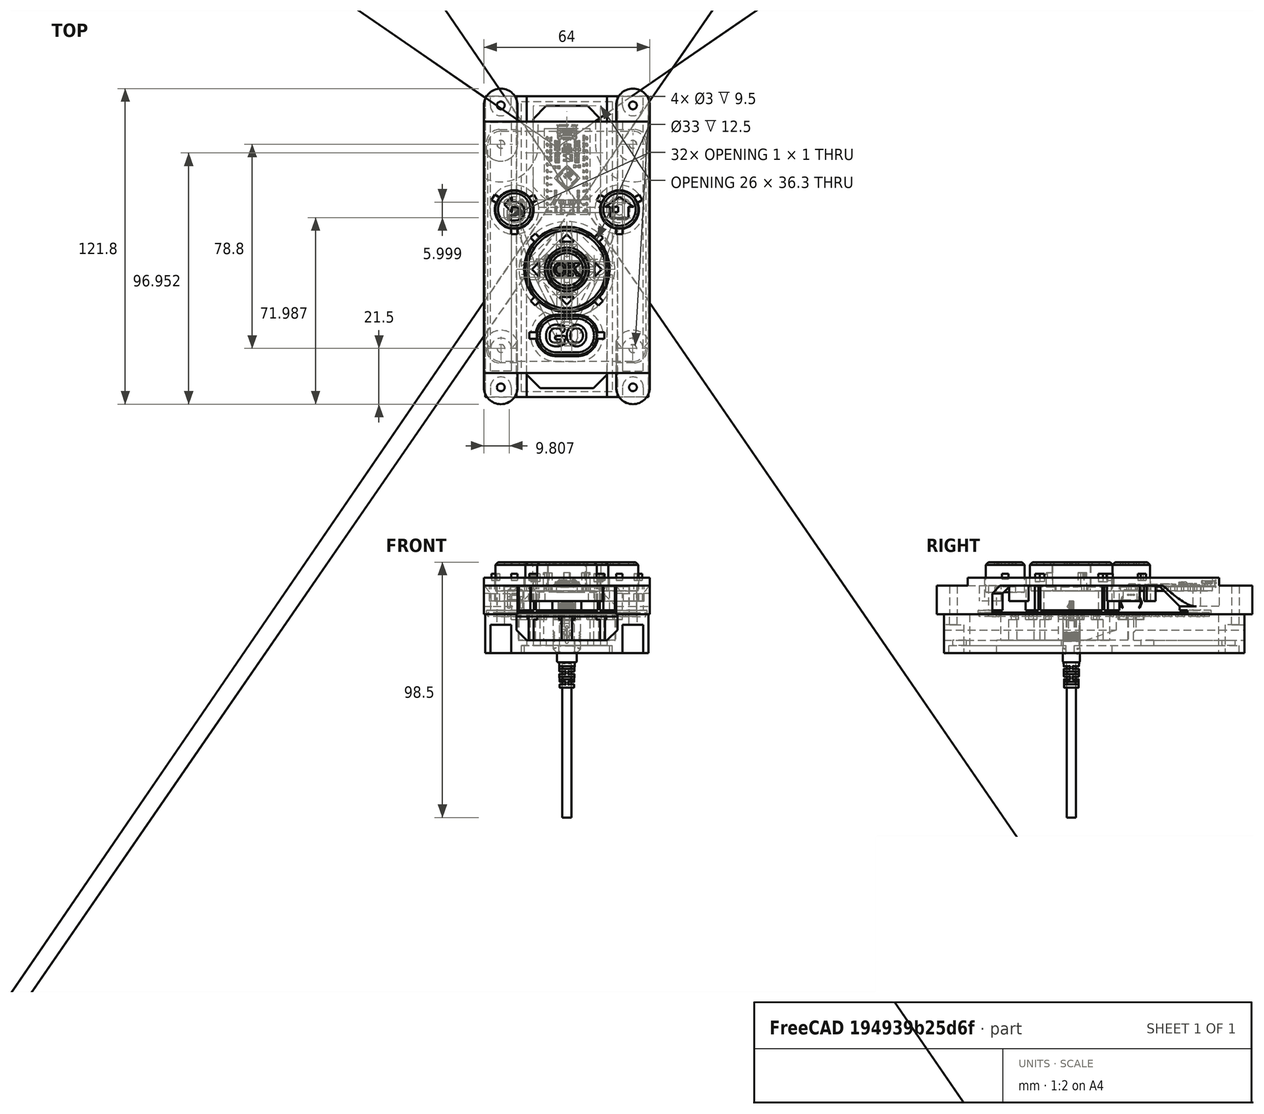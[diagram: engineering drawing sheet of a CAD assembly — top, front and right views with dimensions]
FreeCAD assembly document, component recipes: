
FREECAD ASSEMBLY — COMPONENT RECIPES ("NavigationBoard")

This assembly document has 11 components, labeled P0..P10 below (a component is one placed body or linked part). 7 of them carry a construction recipe — the FreeCAD feature program that regenerates the part from scratch, quoted from this document or its linked companion documents; the rest are supplied as boundary geometry only. No exploded tour is included for this assembly.
COMPONENT P0 — recipe-attached ("BoardHolder", modeled in this document).
Construction recipe (the document's own serialized feature program — sketch geometry with constraints, then the solid features built on it; lengths are millimeters unless a unit is written):

FEATURE [Sketcher::SketchObject] Sketch046
  ArcFitTolerance = 1e-06
  AttachmentSupport = -> [XY_Plane011]
  FullyConstrained = true
  MakeInternals = false
  MapMode = 5
  sketch-geometry (5):
    g0: LineSegment StartX=-31.5 StartY=-58 StartZ=0 EndX=31.5 EndY=-58 EndZ=0
    g1: LineSegment StartX=31.5 StartY=-58 StartZ=0 EndX=31.5 EndY=58 EndZ=0
    g2: LineSegment StartX=31.5 StartY=58 StartZ=0 EndX=-31.5 EndY=58 EndZ=0
    g3: LineSegment StartX=-31.5 StartY=58 StartZ=0 EndX=-31.5 EndY=-58 EndZ=0
    g4: GeomPoint [constr] X=0 Y=0 Z=0
  constraints (12):
    c: Coincident(g0,g1)
    c: Coincident(g1,g2)
    c: Coincident(g2,g3)
    c: Coincident(g3,g0)
    c: Horizontal(g0)
    c: Horizontal(g2)
    c: Vertical(g1)
    c: Vertical(g3)
    c: Symmetric(g2,g0,g4)
    c: Distance(g1,g3) = 63
    c: Distance(g0,g2) = 116
    c: Coincident(g4,g-1)
FEATURE [PartDesign::Pad] Pad025
  Direction = (0,0,1)
  Length = 5
  Length2 = 10
  Profile = -> Sketch046
  ReferenceAxis = -> Sketch046 [N_Axis]
  Refine = true
  Suppressed = false
  Type = 0
FEATURE [Sketcher::SketchObject] Sketch047
  ArcFitTolerance = 1e-06
  AttachmentSupport = -> [Pad025]
  FullyConstrained = true
  MakeInternals = false
  MapMode = 5
  Placement = pos=(0,0,5) rot=(0,0,1;0rad)
  sketch-geometry (8):
    g0: Circle CenterX=-20.3 CenterY=14.22 CenterZ=0 NormalX=0 NormalY=0 NormalZ=1 AngleXU=0 Radius=2
    g1: Circle CenterX=20.3 CenterY=14.22 CenterZ=0 NormalX=0 NormalY=0 NormalZ=1 AngleXU=0 Radius=2
    g2: Circle CenterX=0 CenterY=3.9 CenterZ=0 NormalX=0 NormalY=0 NormalZ=1 AngleXU=0 Radius=2
    g3: Circle CenterX=-12.7 CenterY=-8.8 CenterZ=0 NormalX=0 NormalY=0 NormalZ=1 AngleXU=0 Radius=2
    g4: Circle CenterX=0 CenterY=-8.8 CenterZ=0 NormalX=0 NormalY=0 NormalZ=1 AngleXU=0 Radius=2
    g5: Circle CenterX=12.7 CenterY=-8.8 CenterZ=0 NormalX=0 NormalY=0 NormalZ=1 AngleXU=0 Radius=2
    g6: Circle CenterX=0 CenterY=-21.5 CenterZ=0 NormalX=0 NormalY=0 NormalZ=1 AngleXU=0 Radius=2
    g7: Circle CenterX=0 CenterY=-34.1 CenterZ=0 NormalX=0 NormalY=0 NormalZ=1 AngleXU=0 Radius=2
  constraints (24):
    c: Diameter(g0) = 4
    c: DistanceX(g0,g-1) = 20.3
    c: Distance(g0,g-1) = 14.22
    c: Diameter(g1) = 4
    c: DistanceX(g-1,g1) = 20.3
    c: Distance(g1,g-1) = 14.22
    c: Diameter(g2) = 4
    c: PointOnObject(g2,g-2)
    c: DistanceY(g-1,g2) = 3.9
    c: Diameter(g3) = 4
    c: Diameter(g4) = 4
    c: PointOnObject(g4,g-2)
    c: Diameter(g5) = 4
    c: Distance(g3,g-2) = 12.7
    c: DistanceY(g3,g-1) = 8.8
    c: Horizontal(g3,g4)
    c: Horizontal(g4,g5)
    c: DistanceX(g-1,g5) = 12.7
    c: Diameter(g6) = 4
    c: PointOnObject(g6,g-2)
    c: Diameter(g7) = 4
    c: PointOnObject(g7,g-2)
    c: DistanceY(g6,g-1) = 21.5
    c: DistanceY(g7,g6) = 12.6
FEATURE [PartDesign::Pad] Pad026
  BaseFeature = -> Pad025
  Direction = (0,0,1)
  Length = 10
  Length2 = 10
  Profile = -> Sketch047
  ReferenceAxis = -> Sketch047 [N_Axis]
  Refine = true
  Suppressed = false
  Type = 0
FEATURE [Sketcher::SketchObject] Sketch048
  ArcFitTolerance = 1e-06
  AttachmentSupport = -> [Pad026]
  ExternalGeometry = -> [Pad026]
  FullyConstrained = false
  MakeInternals = false
  MapMode = 5
  Placement = pos=(0,0,5) rot=(0,0,1;0rad)
  sketch-geometry (15):
    g0: LineSegment StartX=-13.6496 StartY=-9.1135 StartZ=0 EndX=-21.2496 EndY=13.9065 EndZ=0
    g1: ArcOfCircle CenterX=-20.3 CenterY=14.22 CenterZ=0 NormalX=0 NormalY=0 NormalZ=1 AngleXU=0 Radius=1 StartAngle=1.5708 EndAngle=3.46047
    g2: LineSegment StartX=-20.3 StartY=15.22 StartZ=0 EndX=20.3 EndY=15.22 EndZ=0
    g3: ArcOfCircle CenterX=20.3 CenterY=14.22 CenterZ=0 NormalX=0 NormalY=0 NormalZ=1 AngleXU=-1.88968 Radius=1 StartAngle=1.5708 EndAngle=3.46047
    g4: LineSegment StartX=21.2496 StartY=13.9065 StartZ=0 EndX=13.6496 EndY=-9.1135 EndZ=0
    g5: ArcOfCircle CenterX=12.7 CenterY=-8.8 CenterZ=0 NormalX=0 NormalY=0 NormalZ=1 AngleXU=-2.03602 Radius=1 StartAngle=1.5708 EndAngle=1.71714
    g6: LineSegment StartX=13.5937 StartY=-9.24863 StartZ=0 EndX=0.89372 EndY=-34.5486 EndZ=0
    g7: ArcOfCircle CenterX=0 CenterY=-34.1 CenterZ=0 NormalX=0 NormalY=0 NormalZ=1 AngleXU=2.03602 Radius=1 StartAngle=1.5708 EndAngle=3.78193
    g8: LineSegment StartX=-0.89372 StartY=-34.5486 StartZ=0 EndX=-13.5937 EndY=-9.24863 EndZ=0
    g9: ArcOfCircle CenterX=-12.7 CenterY=-8.8 CenterZ=0 NormalX=0 NormalY=0 NormalZ=1 AngleXU=1.88968 Radius=1 StartAngle=1.5708 EndAngle=1.71714
    g10: LineSegment StartX=-11.7734 StartY=-8.41689 StartZ=0 EndX=-18.9168 EndY=13.22 EndZ=0
    g11: LineSegment StartX=-18.9168 StartY=13.22 StartZ=0 EndX=18.9168 EndY=13.22 EndZ=0
    g12: LineSegment StartX=18.9168 StartY=13.22 StartZ=0 EndX=11.7734 EndY=-8.41689 EndZ=0
    g13: LineSegment StartX=11.7734 StartY=-8.41689 StartZ=0 EndX=-1.8e-15 EndY=-31.871 EndZ=0
    g14: LineSegment StartX=-1.8e-15 StartY=-31.871 StartZ=0 EndX=-11.7734 EndY=-8.41689 EndZ=0
  constraints (15):
    c: Tangent(g0,g1) = 1.5708
    c: Tangent(g0,g9) = 1.5708
    c: Tangent(g1,g2) = 1.5708
    c: Tangent(g2,g3) = 1.5708
    c: Tangent(g3,g4) = 1.5708
    c: Tangent(g4,g5) = 1.5708
    c: Tangent(g5,g6) = 1.5708
    c: Tangent(g6,g7) = 1.5708
    c: Tangent(g7,g8) = 1.5708
    c: Tangent(g8,g9) = 1.5708
    c: Coincident(g10,g11)
    c: Coincident(g10,g14)
    c: Coincident(g11,g12)
    c: Coincident(g12,g13)
    c: Coincident(g13,g14)
FEATURE [PartDesign::Pad] Pad027
  BaseFeature = -> Pad026
  Direction = (0,0,1)
  Length = 10
  Length2 = 10
  Profile = -> Sketch048
  ReferenceAxis = -> Sketch048 [N_Axis]
  Refine = true
  Suppressed = false
  Type = 0
FEATURE [Sketcher::SketchObject] Sketch049
  ArcFitTolerance = 1e-06
  AttachmentSupport = -> [Pad027]
  ExternalGeometry = -> [Pad027]
  FullyConstrained = false
  MakeInternals = false
  MapMode = 5
  Placement = pos=(0,0,5) rot=(0,0,1;0rad)
  sketch-geometry (12):
    g0: LineSegment StartX=-13.4071 StartY=-9.50711 StartZ=0 EndX=-0.707107 EndY=-22.2071 EndZ=0
    g1: ArcOfCircle CenterX=0 CenterY=-21.5 CenterZ=0 NormalX=0 NormalY=0 NormalZ=-1 AngleXU=2.35619 Radius=1 StartAngle=1.5708 EndAngle=3.14159
    g2: LineSegment StartX=0.707107 StartY=-22.2071 StartZ=0 EndX=13.4071 EndY=-9.50711 EndZ=0
    g3: ArcOfCircle CenterX=12.7 CenterY=-8.8 CenterZ=0 NormalX=0 NormalY=0 NormalZ=-1 AngleXU=0.785398 Radius=1 StartAngle=1.5708 EndAngle=3.14159
    g4: LineSegment StartX=13.4071 StartY=-8.09289 StartZ=0 EndX=0.707107 EndY=4.60711 EndZ=0
    g5: ArcOfCircle CenterX=0 CenterY=3.9 CenterZ=0 NormalX=0 NormalY=0 NormalZ=-1 AngleXU=-0.785398 Radius=1 StartAngle=1.5708 EndAngle=3.14159
    g6: LineSegment StartX=-0.707107 StartY=4.60711 StartZ=0 EndX=-13.4071 EndY=-8.09289 EndZ=0
    g7: ArcOfCircle CenterX=-12.7 CenterY=-8.8 CenterZ=0 NormalX=0 NormalY=0 NormalZ=-1 AngleXU=-2.35619 Radius=1 StartAngle=1.5708 EndAngle=3.14159
    g8: LineSegment StartX=-11.2858 StartY=-8.8 StartZ=0 EndX=0 EndY=-20.0858 EndZ=0
    g9: LineSegment StartX=0 StartY=-20.0858 StartZ=0 EndX=11.2858 EndY=-8.8 EndZ=0
    g10: LineSegment StartX=11.2858 StartY=-8.8 StartZ=0 EndX=0 EndY=2.48579 EndZ=0
    g11: LineSegment StartX=0 StartY=2.48579 StartZ=0 EndX=-11.2858 EndY=-8.8 EndZ=0
  constraints (12):
    c: Tangent(g0,g1) = -1.5708
    c: Tangent(g0,g7) = -1.5708
    c: Tangent(g1,g2) = -1.5708
    c: Tangent(g2,g3) = -1.5708
    c: Tangent(g3,g4) = -1.5708
    c: Tangent(g4,g5) = -1.5708
    c: Tangent(g5,g6) = -1.5708
    c: Tangent(g6,g7) = -1.5708
    c: Coincident(g8,g9)
    c: Coincident(g8,g11)
    c: Coincident(g9,g10)
    c: Coincident(g10,g11)
FEATURE [PartDesign::Pad] Pad028
  BaseFeature = -> Pad027
  Direction = (0,0,1)
  Length = 10
  Length2 = 10
  Profile = -> Sketch049
  ReferenceAxis = -> Sketch049 [N_Axis]
  Refine = true
  Suppressed = false
  Type = 0
FEATURE [Sketcher::SketchObject] Sketch050
  ArcFitTolerance = 1e-06
  AttachmentSupport = -> [Pad028]
  ExternalGeometry = -> [Pad028]
  FullyConstrained = false
  MakeInternals = false
  MapMode = 5
  Placement = pos=(0,0,5) rot=(0,0,1;0rad)
  sketch-geometry (6):
    g0: ArcOfCircle CenterX=0 CenterY=3.9 CenterZ=0 NormalX=0 NormalY=0 NormalZ=-1 AngleXU=-1.5708 Radius=1 StartAngle=1.5708 EndAngle=4.71239
    g1: LineSegment StartX=1 StartY=3.9 StartZ=0 EndX=1 EndY=-8.76667 EndZ=0
    g2: LineSegment StartX=1 StartY=-8.76667 StartZ=0 EndX=1 EndY=-34.1 EndZ=0
    g3: ArcOfCircle CenterX=0 CenterY=-34.1 CenterZ=0 NormalX=0 NormalY=0 NormalZ=-1 AngleXU=1.5708 Radius=1 StartAngle=1.5708 EndAngle=4.71239
    g4: LineSegment StartX=-1 StartY=-8.76667 StartZ=0 EndX=-1 EndY=-34.1 EndZ=0
    g5: LineSegment StartX=-1 StartY=3.9 StartZ=0 EndX=-1 EndY=-8.76667 EndZ=0
  constraints (6):
    c: Tangent(g0,g1) = 1.5708
    c: Tangent(g0,g5) = -1.5708
    c: Coincident(g1,g2)
    c: Tangent(g2,g3) = 1.5708
    c: Tangent(g3,g4) = -1.5708
    c: Coincident(g4,g5)
FEATURE [PartDesign::Pad] Pad029
  BaseFeature = -> Pad028
  Direction = (0,0,1)
  Length = 10
  Length2 = 10
  Profile = -> Sketch050
  ReferenceAxis = -> Sketch050 [N_Axis]
  Refine = true
  Suppressed = false
  Type = 0
FEATURE [Sketcher::SketchObject] Sketch051
  ArcFitTolerance = 1e-06
  AttachmentSupport = -> [Pad029]
  ExternalGeometry = -> [Pad029]
  FullyConstrained = false
  MakeInternals = false
  MapMode = 5
  Placement = pos=(0,0,5) rot=(0,0,1;0rad)
  sketch-geometry (6):
    g0: ArcOfCircle CenterX=-12.7 CenterY=-8.8 CenterZ=0 NormalX=0 NormalY=0 NormalZ=-1 AngleXU=-3.14159 Radius=1 StartAngle=1.5708 EndAngle=4.71239
    g1: LineSegment StartX=-12.7 StartY=-7.8 StartZ=0 EndX=-4.23333 EndY=-7.8 EndZ=0
    g2: LineSegment StartX=-4.23333 StartY=-7.8 StartZ=0 EndX=12.7 EndY=-7.8 EndZ=0
    g3: ArcOfCircle CenterX=12.7 CenterY=-8.8 CenterZ=0 NormalX=0 NormalY=0 NormalZ=-1 AngleXU=0 Radius=1 StartAngle=1.5708 EndAngle=4.71239
    g4: LineSegment StartX=-4.23333 StartY=-9.8 StartZ=0 EndX=12.7 EndY=-9.8 EndZ=0
    g5: LineSegment StartX=-12.7 StartY=-9.8 StartZ=0 EndX=-4.23333 EndY=-9.8 EndZ=0
  constraints (6):
    c: Tangent(g0,g1) = 1.5708
    c: Tangent(g0,g5) = -1.5708
    c: Coincident(g1,g2)
    c: Tangent(g2,g3) = 1.5708
    c: Tangent(g3,g4) = -1.5708
    c: Coincident(g4,g5)
FEATURE [PartDesign::Pad] Pad030
  BaseFeature = -> Pad029
  Direction = (0,0,1)
  Length = 10
  Length2 = 10
  Profile = -> Sketch051
  ReferenceAxis = -> Sketch051 [N_Axis]
  Refine = true
  Suppressed = false
  Type = 0
FEATURE [Sketcher::SketchObject] Sketch052
  ArcFitTolerance = 1e-06
  AttachmentSupport = -> [Pad030]
  ExternalGeometry = -> [Pad030]
  FullyConstrained = true
  MakeInternals = false
  MapMode = 5
  Placement = pos=(0,0,15) rot=(0,0,1;0rad)
  sketch-geometry (16):
    g0: Circle CenterX=-20.3 CenterY=14.22 CenterZ=0 NormalX=0 NormalY=0 NormalZ=1 AngleXU=0 Radius=5
    g1: Circle CenterX=20.3 CenterY=14.22 CenterZ=0 NormalX=0 NormalY=0 NormalZ=1 AngleXU=0 Radius=5
    g2: Circle CenterX=0 CenterY=3.9 CenterZ=0 NormalX=0 NormalY=0 NormalZ=1 AngleXU=0 Radius=5
    g3: Circle CenterX=-12.7 CenterY=-8.8 CenterZ=0 NormalX=0 NormalY=0 NormalZ=1 AngleXU=0 Radius=5
    g4: Circle CenterX=0 CenterY=-8.8 CenterZ=0 NormalX=0 NormalY=0 NormalZ=1 AngleXU=0 Radius=5
    g5: Circle CenterX=12.7 CenterY=-8.8 CenterZ=0 NormalX=0 NormalY=0 NormalZ=1 AngleXU=0 Radius=5
    g6: Circle CenterX=0 CenterY=-21.5 CenterZ=0 NormalX=0 NormalY=0 NormalZ=1 AngleXU=0 Radius=5
    g7: Circle CenterX=-20.3 CenterY=14.22 CenterZ=0 NormalX=0 NormalY=0 NormalZ=1 AngleXU=0 Radius=2
    g8: Circle CenterX=20.3 CenterY=14.22 CenterZ=0 NormalX=0 NormalY=0 NormalZ=1 AngleXU=0 Radius=2
    g9: Circle CenterX=0 CenterY=3.9 CenterZ=0 NormalX=0 NormalY=0 NormalZ=1 AngleXU=0 Radius=2
    g10: Circle CenterX=-12.7 CenterY=-8.8 CenterZ=0 NormalX=0 NormalY=0 NormalZ=1 AngleXU=0 Radius=2
    g11: Circle CenterX=0 CenterY=-8.8 CenterZ=0 NormalX=0 NormalY=0 NormalZ=1 AngleXU=0 Radius=2
    g12: Circle CenterX=12.7 CenterY=-8.8 CenterZ=0 NormalX=0 NormalY=0 NormalZ=1 AngleXU=0 Radius=2
    g13: Circle CenterX=0 CenterY=-21.5 CenterZ=0 NormalX=0 NormalY=0 NormalZ=1 AngleXU=0 Radius=2
    g14: Circle CenterX=0 CenterY=-34.1 CenterZ=0 NormalX=0 NormalY=0 NormalZ=1 AngleXU=0 Radius=5
    g15: Circle CenterX=0 CenterY=-34.1 CenterZ=0 NormalX=0 NormalY=0 NormalZ=1 AngleXU=0 Radius=2
  constraints (32):
    c: Diameter(g0) = 10
    c: Coincident(g0,g-3)
    c: Diameter(g1) = 10
    c: Coincident(g1,g-4)
    c: Diameter(g2) = 10
    c: Coincident(g2,g-5)
    c: Diameter(g3) = 10
    c: Coincident(g3,g-6)
    c: Diameter(g4) = 10
    c: Coincident(g4,g-8)
    c: Diameter(g5) = 10
    c: Coincident(g5,g-7)
    c: Diameter(g6) = 10
    c: Coincident(g6,g-9)
    c: Diameter(g7) = 4
    c: Coincident(g7,g0)
    c: Diameter(g8) = 4
    c: Coincident(g8,g1)
    c: Diameter(g9) = 4
    c: Coincident(g9,g2)
    c: Diameter(g10) = 4
    c: Coincident(g10,g3)
    c: Diameter(g11) = 4
    c: Coincident(g11,g4)
    c: Diameter(g12) = 4
    c: Coincident(g12,g5)
    c: Diameter(g13) = 4
    c: Coincident(g13,g6)
    c: Diameter(g14) = 10
    c: Coincident(g14,g-10)
    c: Diameter(g15) = 4
    c: Coincident(g15,g14)
FEATURE [Sketcher::SketchObject] Sketch053
  ArcFitTolerance = 1e-06
  AttachmentSupport = -> [Pad030]
  FullyConstrained = true
  MakeInternals = false
  MapMode = 5
  Placement = pos=(31.5,0,0) rot=(0.57735,0.57735,0.57735;2.0944rad)
  sketch-geometry (4):
    g0: LineSegment StartX=-58 StartY=15 StartZ=0 EndX=-58 EndY=5 EndZ=0
    g1: LineSegment StartX=-58 StartY=5 StartZ=0 EndX=58 EndY=5 EndZ=0
    g2: LineSegment StartX=58 StartY=15 StartZ=0 EndX=-58 EndY=15 EndZ=0
    g3: LineSegment StartX=58 StartY=15 StartZ=0 EndX=58 EndY=5 EndZ=0
  constraints (12):
    c: Vertical(g0)
    c: PointOnObject(g1,g-3)
    c: PointOnObject(g1,g-3)
    c: Coincident(g2,g0)
    c: Horizontal(g2)
    c: Distance(g-2,g0) = 58
    c: Vertical(g3)
    c: DistanceY(g1,g2) = 10
    c: Distance(g-2,g3) = 58
    c: Coincident(g2,g3)
    c: Coincident(g0,g1)
    c: Coincident(g3,g1)
FEATURE [PartDesign::Pad] Pad031
  BaseFeature = -> Pad030
  Direction = (1,0,0)
  Length = 12
  Length2 = 10
  Profile = -> Sketch053
  ReferenceAxis = -> Sketch053 [N_Axis]
  Refine = true
  Reversed = true
  Suppressed = false
  Type = 0
FEATURE [Sketcher::SketchObject] Sketch054
  ArcFitTolerance = 1e-06
  AttachmentSupport = -> [Pad031]
  ExternalGeometry = -> [Pad031]
  FullyConstrained = true
  MakeInternals = false
  MapMode = 5
  Placement = pos=(0,0,15) rot=(0,0,1;0rad)
  sketch-geometry (6):
    g0: LineSegment StartX=21.5 StartY=48 StartZ=0 EndX=21.5 EndY=-48 EndZ=0
    g1: LineSegment StartX=21.5 StartY=-48 StartZ=0 EndX=29.5 EndY=-48 EndZ=0
    g2: LineSegment StartX=29.5 StartY=-48 StartZ=0 EndX=29.5 EndY=48 EndZ=0
    g3: LineSegment StartX=29.5 StartY=48 StartZ=0 EndX=21.5 EndY=48 EndZ=0
    g4: Circle CenterX=25.5 CenterY=-54.3 CenterZ=0 NormalX=0 NormalY=0 NormalZ=1 AngleXU=0 Radius=1.5
    g5: Circle CenterX=25.5 CenterY=54.5 CenterZ=0 NormalX=0 NormalY=0 NormalZ=1 AngleXU=0 Radius=1.5
  constraints (18):
    c: Coincident(g0,g1)
    c: Coincident(g1,g2)
    c: Coincident(g2,g3)
    c: Coincident(g3,g0)
    c: Vertical(g0)
    c: Vertical(g2)
    c: Horizontal(g1)
    c: Horizontal(g3)
    c: Distance(g-5,g3) = 10
    c: Distance(g-4,g0) = 2
    c: Distance(g-3,g2) = 2
    c: Distance(g-3,g1) = 10
    c: Diameter(g4) = 3
    c: Distance(g4,g-3) = 6
    c: DistanceY(g4,g1) = 6.3
    c: Diameter(g5) = 3
    c: Distance(g5,g-4) = 6
    c: Distance(g5,g3) = 6.5
FEATURE [PartDesign::Pocket] Pocket023
  BaseFeature = -> Pad031
  Direction = (0,0,-1)
  Length = 5
  Length2 = 5
  Profile = -> Sketch054
  ReferenceAxis = -> Sketch054 [N_Axis]
  Refine = true
  Suppressed = false
  Type = 1
FEATURE [Sketcher::SketchObject] Sketch055
  ArcFitTolerance = 1e-06
  AttachmentSupport = -> [Pocket023]
  ExternalGeometry = -> [Pocket023]
  FullyConstrained = true
  MakeInternals = false
  MapMode = 5
  Placement = pos=(0,0,0) rot=(1,0,0;3.14159rad)
  sketch-geometry (8):
    g0: ArcOfCircle CenterX=25.5 CenterY=54.3 CenterZ=0 NormalX=0 NormalY=0 NormalZ=1 AngleXU=0 Radius=4 StartAngle=3.14159 EndAngle=6.28319
    g1: ArcOfCircle CenterX=25.5 CenterY=62.3 CenterZ=0 NormalX=0 NormalY=0 NormalZ=1 AngleXU=0 Radius=4 StartAngle=0 EndAngle=3.14159
    g2: LineSegment StartX=21.5 StartY=54.3 StartZ=0 EndX=21.5 EndY=62.3 EndZ=0
    g3: LineSegment StartX=29.5 StartY=54.3 StartZ=0 EndX=29.5 EndY=62.3 EndZ=0
    g4: ArcOfCircle CenterX=25.5 CenterY=-54.5 CenterZ=0 NormalX=0 NormalY=0 NormalZ=1 AngleXU=0 Radius=4 StartAngle=-9e-16 EndAngle=3.14159
    g5: ArcOfCircle CenterX=25.5 CenterY=-62.5 CenterZ=0 NormalX=0 NormalY=0 NormalZ=1 AngleXU=0 Radius=4 StartAngle=3.14159 EndAngle=6.28319
    g6: LineSegment StartX=29.5 StartY=-54.5 StartZ=0 EndX=29.5 EndY=-62.5 EndZ=0
    g7: LineSegment StartX=21.5 StartY=-54.5 StartZ=0 EndX=21.5 EndY=-62.5 EndZ=0
  constraints (20):
    c: Tangent(g0,g2) = 1.5708
    c: Tangent(g0,g3) = -1.5708
    c: Tangent(g1,g2) = 1.5708
    c: Tangent(g1,g3) = -1.5708
    c: Equal(g0,g1)
    c: Vertical(g3)
    c: Distance(g0,g1) = 8
    c: Radius(g0) = 4
    c: Distance(g0,g-3) = 4
    c: DistanceY(g-3,g0) = 6.3
    c: Tangent(g4,g6) = 1.5708
    c: Tangent(g4,g7) = -1.5708
    c: Tangent(g5,g6) = 1.5708
    c: Tangent(g5,g7) = -1.5708
    c: Equal(g4,g5)
    c: Vertical(g7)
    c: Distance(g4,g5) = 8
    c: Radius(g4) = 4
    c: Distance(g4,g-4) = 4
    c: DistanceY(g4,g-4) = 6.5
FEATURE [PartDesign::Pocket] Pocket024
  BaseFeature = -> Pocket023
  Direction = (0,0,1)
  Length = 11
  Length2 = 5
  Profile = -> Sketch055
  ReferenceAxis = -> Sketch055 [N_Axis]
  Refine = true
  Suppressed = false
  Type = 0
FEATURE [PartDesign::Pocket] Pocket025
  BaseFeature = -> Pocket024
  Direction = (0,0,-1)
  Length = 2
  Length2 = 5
  Profile = -> Sketch052
  ReferenceAxis = -> Sketch052 [N_Axis]
  Refine = true
  Suppressed = false
  Type = 0
FEATURE [Sketcher::SketchObject] Sketch056
  ArcFitTolerance = 1e-06
  AttachmentSupport = -> [Pocket025]
  ExternalGeometry = -> [Pocket025]
  FullyConstrained = false
  MakeInternals = false
  MapMode = 5
  Placement = pos=(0,0,0) rot=(1,0,0;3.14159rad)
  sketch-geometry (14):
    g0: LineSegment StartX=-17.5 StartY=56 StartZ=0 EndX=-17.5 EndY=10.8104 EndZ=0
    g1: LineSegment StartX=-17.5 StartY=-56 StartZ=0 EndX=17.5 EndY=-56 EndZ=0
    g2: LineSegment StartX=17.5 StartY=-56 StartZ=0 EndX=17.5 EndY=7.59482 EndZ=0
    g3: LineSegment StartX=17.5 StartY=56 StartZ=0 EndX=-17.5 EndY=56 EndZ=0
    g4: LineSegment StartX=-3 StartY=37.6173 StartZ=0 EndX=3 EndY=37.6173 EndZ=0
    g5: LineSegment StartX=3 StartY=37.6173 StartZ=0 EndX=16.4564 EndY=10.8104 EndZ=0
    g6: LineSegment StartX=16.4564 StartY=10.8104 StartZ=0 EndX=17.5 EndY=10.8104 EndZ=0
    g7: LineSegment StartX=-3 StartY=37.6173 StartZ=0 EndX=-16.4564 EndY=10.8104 EndZ=0
    g8: LineSegment StartX=-16.4564 StartY=10.8104 StartZ=0 EndX=-17.5 EndY=10.8104 EndZ=0
    g9: LineSegment StartX=-17.5 StartY=7.59482 StartZ=0 EndX=-3 EndY=-6.90518 EndZ=0
    g10: LineSegment StartX=-3 StartY=-6.90518 StartZ=0 EndX=3 EndY=-6.90518 EndZ=0
    g11: LineSegment StartX=3 StartY=-6.90518 StartZ=0 EndX=17.5 EndY=7.59482 EndZ=0
    g12: LineSegment StartX=-17.5 StartY=7.59482 StartZ=0 EndX=-17.5 EndY=-56 EndZ=0
    g13: LineSegment StartX=17.5 StartY=10.8104 StartZ=0 EndX=17.5 EndY=56 EndZ=0
  constraints (37):
    c: Coincident(g12,g1)
    c: Coincident(g1,g2)
    c: Coincident(g13,g3)
    c: Coincident(g3,g0)
    c: Vertical(g0)
    c: Vertical(g2)
    c: Horizontal(g1)
    c: Horizontal(g3)
    c: Distance(g-3,g3) = 2
    c: Distance(g-4,g0) = 2
    c: Distance(g-3,g2) = 4
    c: Distance(g-5,g1) = 2
    c: Horizontal(g4)
    c: Coincident(g4,g5)
    c: Coincident(g5,g6)
    c: PointOnObject(g6,g13)
    c: Coincident(g4,g7)
    c: Coincident(g7,g8)
    c: PointOnObject(g9,g12)
    c: Coincident(g9,g10)
    c: Horizontal(g10)
    c: Coincident(g10,g11)
    c: Angle(g11,g2) = 0.785398
    c: Angle(g0,g9) = 0.785398
    c: Distance(g9,g-2) = 3
    c: Distance(g10,g-2) = 3
    c: Horizontal(g8)
    c: Horizontal(g6)
    c: Horizontal(g5,g7)
    c: Distance(g4,g-2) = 3
    c: Distance(g4,g-2) = 3
    c: Coincident(g0,g8)
    c: PointOnObject(g12,g9)
    c: Coincident(g2,g11)
    c: PointOnObject(g13,g6)
    c: Parallel(g7,g-7)
    c: Parallel(g5,g-6)
FEATURE [PartDesign::Chamfer] Chamfer012
  Angle = 45
  Base = -> Pocket025 [Edge34,Edge47]
  BaseFeature = -> Pocket025
  ChamferType = 0
  FlipDirection = false
  Refine = true
  Size = 4
  Size2 = 1
  SupportTransform = false
  Suppressed = false
  UseAllEdges = false
FEATURE [PartDesign::Mirrored] Mirrored001
  BaseFeature = -> Chamfer012
  MirrorPlane = -> YZ_Plane011
  Originals = -> [Pad031,Pocket023,Pocket024,Pocket025,Chamfer012]
  Refine = true
  Suppressed = false
  TransformMode = 0
FEATURE [PartDesign::Pocket] Pocket026
  BaseFeature = -> Mirrored001
  Direction = (0,0,1)
  Length = 3
  Length2 = 5
  Profile = -> Sketch056
  ReferenceAxis = -> Sketch056 [N_Axis]
  Refine = true
  Suppressed = false
  Type = 0
FEATURE [Sketcher::SketchObject] Sketch057
  ArcFitTolerance = 1e-06
  AttachmentSupport = -> [Pocket026]
  ExternalGeometry = -> [Pocket026]
  FullyConstrained = false
  MakeInternals = false
  MapMode = 5
  Placement = pos=(0,0,5) rot=(0,0,1;0rad)
  sketch-geometry (16):
    g0: LineSegment StartX=-15.5 StartY=-12.7157 StartZ=0 EndX=-3 EndY=-37.6173 EndZ=0
    g1: LineSegment StartX=-3 StartY=-37.6173 StartZ=0 EndX=3 EndY=-37.6173 EndZ=0
    g2: LineSegment StartX=3 StartY=-37.6173 StartZ=0 EndX=15.5 EndY=-12.7157 EndZ=0
    g3: LineSegment StartX=15.5 StartY=-12.7157 StartZ=0 EndX=15.5 EndY=-49.4189 EndZ=0
    g4: LineSegment StartX=15.5 StartY=-49.4189 StartZ=0 EndX=10.3017 EndY=-54.6173 EndZ=0
    g5: LineSegment StartX=10.3017 StartY=-54.6173 StartZ=0 EndX=-10.3017 EndY=-54.6173 EndZ=0
    g6: LineSegment StartX=-10.3017 StartY=-54.6173 StartZ=0 EndX=-15.5 EndY=-49.4189 EndZ=0
    g7: LineSegment StartX=-15.5 StartY=-49.4189 StartZ=0 EndX=-15.5 EndY=-12.7157 EndZ=0
    g8: LineSegment StartX=-13 StartY=49.3033 StartZ=0 EndX=-8 EndY=54.3033 EndZ=0
    g9: LineSegment StartX=-8 StartY=54.3033 StartZ=0 EndX=8 EndY=54.3033 EndZ=0
    g10: LineSegment StartX=8 StartY=54.3033 StartZ=0 EndX=13 EndY=49.3033 EndZ=0
    g11: LineSegment StartX=13 StartY=49.3033 StartZ=0 EndX=13 EndY=23 EndZ=0
    g12: LineSegment StartX=13 StartY=23 StartZ=0 EndX=8 EndY=18 EndZ=0
    g13: LineSegment StartX=8 StartY=18 StartZ=0 EndX=-8 EndY=18 EndZ=0
    g14: LineSegment StartX=-8 StartY=18 StartZ=0 EndX=-13 EndY=23 EndZ=0
    g15: LineSegment StartX=-13 StartY=23 StartZ=0 EndX=-13 EndY=49.3033 EndZ=0
  constraints (45):
    c: Coincident(g0,g1)
    c: Horizontal(g1)
    c: Coincident(g1,g2)
    c: Vertical(g3)
    c: Coincident(g3,g4)
    c: Coincident(g4,g5)
    c: Horizontal(g5)
    c: Coincident(g5,g6)
    c: Coincident(g6,g7)
    c: Coincident(g7,g0)
    c: Coincident(g8,g9)
    c: Horizontal(g9)
    c: Coincident(g9,g10)
    c: Coincident(g10,g11)
    c: Vertical(g11)
    c: Coincident(g11,g12)
    c: Coincident(g12,g13)
    c: Horizontal(g13)
    c: Coincident(g13,g14)
    c: Coincident(g14,g15)
    c: Coincident(g15,g8)
    c: Vertical(g15)
    c: Angle(g8,g9) = 2.35619
    c: Angle(g9,g10) = 2.35619
    c: Distance(g8,g-2) = 8
    c: Distance(g9,g-2) = 8
    c: Angle(g13,g14) = 2.35619
    c: Angle(g12,g13) = 2.35619
    c: DistanceX(g13,g-1) = 8
    c: Distance(g12,g-2) = 8
    c: Horizontal(g10,g8)
    c: Distance(g-2,g15) = 13
    c: Distance(g-1,g13) = 18
    c: Vertical(g7)
    c: Angle(g6,g7) = 2.35619
    c: Angle(g3,g4) = 2.35619
    c: Distance(g0,g-2) = 3
    c: Horizontal(g6,g3)
    c: Coincident(g3,g2)
    c: Distance(g1,g5) = 17
    c: Vertical(g-7,g0)
    c: Vertical(g-6,g2)
    c: Coincident(g1,g-4)
    c: Parallel(g2,g-3)
    c: Parallel(g0,g-5)
FEATURE [PartDesign::Pocket] Pocket027
  BaseFeature = -> Pocket026
  Direction = (0,0,-1)
  Length = 5
  Length2 = 5
  Profile = -> Sketch057
  ReferenceAxis = -> Sketch057 [N_Axis]
  Refine = true
  Suppressed = false
  Type = 0
FEATURE [PartDesign::Body] Body  label="BoardHolder"
  AllowCompound = false
  Group = -> [Sketch046,Pad025,Sketch047,Pad026,Sketch048,Pad027,Sketch049,Pad028,Sketch050,Pad029,Sketch051,Pad030,Sketch052,Sketch053,Pad031,Sketch054,Pocket023,Sketch055,Pocket024,Pocket025,Sketch056,Chamfer012,Mirrored001,Pocket026,Sketch057,Pocket027]
  Origin = -> Origin011
  Placement = pos=(0,8.8,-14.1) rot=(0,0,1;0rad)
  Tip = -> Pocket027
COMPONENT P1 — recipe-attached ("NavBoardTop", modeled in this document).
Construction recipe (the document's own serialized feature program — sketch geometry with constraints, then the solid features built on it; lengths are millimeters unless a unit is written):

FEATURE [Sketcher::SketchObject] Sketch001
  ArcFitTolerance = 1e-06
  AttachmentSupport = -> [XY_Plane002]
  FullyConstrained = true
  MakeInternals = false
  MapMode = 5
  sketch-geometry (5):
    g0: LineSegment StartX=-32 StartY=-40 StartZ=0 EndX=32 EndY=-40 EndZ=0
    g1: LineSegment StartX=32 StartY=-40 StartZ=0 EndX=32 EndY=57 EndZ=0
    g2: LineSegment StartX=32 StartY=57 StartZ=0 EndX=-32 EndY=57 EndZ=0
    g3: LineSegment StartX=-32 StartY=57 StartZ=0 EndX=-32 EndY=-40 EndZ=0
    g4: GeomPoint [constr] X=0 Y=0 Z=0
  constraints (13):
    c: Coincident(g0,g1)
    c: Coincident(g1,g2)
    c: Coincident(g2,g3)
    c: Coincident(g3,g0)
    c: Horizontal(g0)
    c: Horizontal(g2)
    c: Vertical(g1)
    c: Vertical(g3)
    c: Coincident(g4,g-1)
    c: Distance(g-1,g2) = 57
    c: Distance(g1,g-2) = 32
    c: Distance(g-1,g0) = 40
    c: Distance(g-2,g3) = 32
FEATURE [PartDesign::Pad] Pad001
  Direction = (0,0,1)
  Length = 3
  Length2 = 10
  Profile = -> Sketch001
  ReferenceAxis = -> Sketch001 [N_Axis]
  Refine = true
  Suppressed = false
  Type = 0
FEATURE [Sketcher::SketchObject] Sketch002
  ArcFitTolerance = 1e-06
  AttachmentSupport = -> [Pad001]
  FullyConstrained = true
  MakeInternals = false
  MapMode = 5
  Placement = pos=(0,0,3) rot=(0,0,1;0rad)
  sketch-geometry (7):
    g0: Circle CenterX=-20.3 CenterY=23.07 CenterZ=0 NormalX=0 NormalY=0 NormalZ=1 AngleXU=0 Radius=7.5
    g1: Circle CenterX=20.3 CenterY=23.07 CenterZ=0 NormalX=0 NormalY=0 NormalZ=1 AngleXU=0 Radius=7.5
    g2: Circle CenterX=0 CenterY=0 CenterZ=0 NormalX=0 NormalY=0 NormalZ=1 AngleXU=0 Radius=16.5
    g3: ArcOfCircle CenterX=-4 CenterY=-25.5 CenterZ=0 NormalX=0 NormalY=0 NormalZ=1 AngleXU=0 Radius=8 StartAngle=1.5708 EndAngle=4.71239
    g4: ArcOfCircle CenterX=4 CenterY=-25.5 CenterZ=0 NormalX=0 NormalY=0 NormalZ=1 AngleXU=0 Radius=8 StartAngle=4.71239 EndAngle=7.85398
    g5: LineSegment StartX=-4 StartY=-17.5 StartZ=0 EndX=4 EndY=-17.5 EndZ=0
    g6: LineSegment StartX=-4 StartY=-33.5 StartZ=0 EndX=4 EndY=-33.5 EndZ=0
  constraints (18):
    c: Diameter(g0) = 15
    c: DistanceX(g0,g-1) = 20.3
    c: DistanceY(g-1,g0) = 23.07
    c: Diameter(g1) = 15
    c: DistanceX(g-1,g1) = 20.3
    c: DistanceY(g-1,g1) = 23.07
    c: Diameter(g2) = 33
    c: Coincident(g2,g-1)
    c: Tangent(g3,g5) = 1.5708
    c: Tangent(g3,g6) = -1.5708
    c: Tangent(g4,g5) = 1.5708
    c: Tangent(g4,g6) = -1.5708
    c: Equal(g3,g4)
    c: Horizontal(g6)
    c: Distance(g3,g4) = 8
    c: Radius(g3) = 8
    c: DistanceY(g4,g-1) = 25.5
    c: Distance(g3,g-2) = 4
FEATURE [Sketcher::SketchObject] Sketch012
  ArcFitTolerance = 1e-06
  AttachmentSupport = -> [Pad001]
  FullyConstrained = true
  MakeInternals = false
  MapMode = 5
  Placement = pos=(0,0,0) rot=(1,0,0;3.14159rad)
  sketch-geometry (6):
    g0: Circle CenterX=-25.4 CenterY=30.5 CenterZ=0 NormalX=0 NormalY=0 NormalZ=1 AngleXU=0 Radius=4
    g1: Circle CenterX=25.4 CenterY=30.5 CenterZ=0 NormalX=0 NormalY=0 NormalZ=1 AngleXU=0 Radius=4
    g2: Circle CenterX=-25.4 CenterY=-48.3 CenterZ=0 NormalX=0 NormalY=0 NormalZ=1 AngleXU=0 Radius=4
    g3: Circle CenterX=25.4 CenterY=-48.3 CenterZ=0 NormalX=0 NormalY=0 NormalZ=1 AngleXU=0 Radius=4
    g4: Circle CenterX=0 CenterY=0 CenterZ=0 NormalX=0 NormalY=0 NormalZ=1 AngleXU=0 Radius=16.5
    g5: Circle CenterX=0 CenterY=0 CenterZ=0 NormalX=0 NormalY=0 NormalZ=1 AngleXU=0 Radius=18.5
  constraints (16):
    c: Diameter(g0) = 8
    c: Diameter(g1) = 8
    c: Diameter(g2) = 8
    c: Diameter(g3) = 8
    c: DistanceX(g0,g-1) = 25.4
    c: DistanceY(g-1,g0) = 30.5
    c: Horizontal(g1,g0)
    c: DistanceX(g-1,g1) = 25.4
    c: Vertical(g2,g0)
    c: Vertical(g1,g3)
    c: Horizontal(g2,g3)
    c: DistanceY(g2,g-1) = 48.3
    c: Diameter(g4) = 33
    c: Coincident(g4,g-1)
    c: Diameter(g5) = 37
    c: Coincident(g5,g4)
FEATURE [PartDesign::Pad] Pad011
  BaseFeature = -> Pad001
  Direction = (0,0,-1)
  Length = 9.5
  Length2 = 10
  Profile = -> Sketch012
  ReferenceAxis = -> Sketch012 [N_Axis]
  Refine = true
  Suppressed = false
  Type = 0
FEATURE [Sketcher::SketchObject] Sketch019
  ArcFitTolerance = 1e-06
  AttachmentSupport = -> [Pad011]
  FullyConstrained = true
  MakeInternals = false
  MapMode = 5
  Placement = pos=(0,0,0) rot=(1,0,0;3.14159rad)
  sketch-geometry (4):
    g0: ArcOfCircle CenterX=-1e-16 CenterY=1e-16 CenterZ=0 NormalX=0 NormalY=0 NormalZ=1 AngleXU=0 Radius=1.5 StartAngle=0.785398 EndAngle=3.92699
    g1: ArcOfCircle CenterX=16.9706 CenterY=-16.9706 CenterZ=0 NormalX=0 NormalY=0 NormalZ=1 AngleXU=0 Radius=1.5 StartAngle=3.92699 EndAngle=7.06858
    g2: LineSegment StartX=1.06066 StartY=1.06066 StartZ=0 EndX=18.0312 EndY=-15.9099 EndZ=0
    g3: LineSegment StartX=-1.06066 StartY=-1.06066 StartZ=0 EndX=15.9099 EndY=-18.0312 EndZ=0
  constraints (9):
    c: Tangent(g0,g2) = 1.5708
    c: Tangent(g0,g3) = -1.5708
    c: Tangent(g1,g2) = 1.5708
    c: Tangent(g1,g3) = -1.5708
    c: Equal(g0,g1)
    c: Distance(g0,g1) = 24
    c: Angle(g-1,g2) = -0.785398
    c: Radius(g0) = 1.5
    c: Coincident(g0,g-1)
FEATURE [PartDesign::Pocket] Pocket003
  BaseFeature = -> Pad011
  Direction = (0,0,1)
  Length = 11
  Length2 = 5
  Profile = -> Sketch019
  ReferenceAxis = -> Sketch019 [N_Axis]
  Refine = true
  Reversed = true
  Suppressed = false
  Type = 1
FEATURE [PartDesign::PolarPattern] PolarPattern
  Angle = 360
  Axis = -> Sketch019 [N_Axis]
  BaseFeature = -> Pocket003
  Mode = 0
  Occurrences = 4
  Offset = 120
  Originals = -> [Pocket003]
  Refine = true
  Suppressed = false
  TransformMode = 0
FEATURE [Sketcher::SketchObject] Sketch020
  ArcFitTolerance = 1e-06
  AttachmentSupport = -> [PolarPattern]
  FullyConstrained = true
  MakeInternals = false
  MapMode = 5
  Placement = pos=(0,0,0) rot=(1,0,0;3.14159rad)
  sketch-geometry (8):
    g0: ArcOfCircle CenterX=-4 CenterY=25.5 CenterZ=0 NormalX=0 NormalY=0 NormalZ=1 AngleXU=0 Radius=8 StartAngle=1.5708 EndAngle=4.71239
    g1: ArcOfCircle CenterX=4 CenterY=25.5 CenterZ=0 NormalX=0 NormalY=0 NormalZ=1 AngleXU=0 Radius=8 StartAngle=4.71239 EndAngle=7.85398
    g2: LineSegment StartX=-4 StartY=33.5 StartZ=0 EndX=4 EndY=33.5 EndZ=0
    g3: LineSegment StartX=-4 StartY=17.5 StartZ=0 EndX=4 EndY=17.5 EndZ=0
    g4: ArcOfCircle CenterX=-4 CenterY=25.5 CenterZ=0 NormalX=0 NormalY=0 NormalZ=1 AngleXU=0 Radius=10 StartAngle=1.5708 EndAngle=4.71239
    g5: ArcOfCircle CenterX=4 CenterY=25.5 CenterZ=0 NormalX=0 NormalY=0 NormalZ=1 AngleXU=0 Radius=10 StartAngle=4.71239 EndAngle=7.85398
    g6: LineSegment StartX=-4 StartY=35.5 StartZ=0 EndX=4 EndY=35.5 EndZ=0
    g7: LineSegment StartX=-4 StartY=15.5 StartZ=0 EndX=4 EndY=15.5 EndZ=0
  constraints (18):
    c: Tangent(g0,g2) = 1.5708
    c: Tangent(g0,g3) = -1.5708
    c: Tangent(g1,g2) = 1.5708
    c: Tangent(g1,g3) = -1.5708
    c: Equal(g0,g1)
    c: Horizontal(g3)
    c: Distance(g0,g1) = 8
    c: Radius(g0) = 8
    c: Distance(g0,g-2) = 4
    c: DistanceY(g-1,g0) = 25.5
    c: Tangent(g4,g6) = 1.5708
    c: Tangent(g4,g7) = -1.5708
    c: Tangent(g5,g6) = 1.5708
    c: Tangent(g5,g7) = -1.5708
    c: Equal(g4,g5)
    c: Coincident(g4,g0)
    c: Coincident(g5,g1)
    c: Radius(g4) = 10
FEATURE [PartDesign::Pad] Pad016
  BaseFeature = -> PolarPattern
  Direction = (0,0,-1)
  Length = 6
  Length2 = 10
  Profile = -> Sketch020
  ReferenceAxis = -> Sketch020 [N_Axis]
  Refine = true
  Suppressed = false
  Type = 0
FEATURE [PartDesign::Pocket] Pocket
  BaseFeature = -> Pad016
  Direction = (0,0,-1)
  Length = 5
  Length2 = 5
  Profile = -> Sketch002
  ReferenceAxis = -> Sketch002 [N_Axis]
  Refine = true
  Suppressed = false
  Type = 1
FEATURE [Sketcher::SketchObject] Sketch022
  ArcFitTolerance = 1e-06
  AttachmentSupport = -> [Pocket]
  ExternalGeometry = -> [Pocket]
  FullyConstrained = true
  MakeInternals = false
  MapMode = 5
  Placement = pos=(0,0,0) rot=(1,0,0;3.14159rad)
  sketch-geometry (4):
    g0: LineSegment StartX=-16 StartY=27 StartZ=0 EndX=-16 EndY=24 EndZ=0
    g1: LineSegment StartX=-16 StartY=24 StartZ=0 EndX=16 EndY=24 EndZ=0
    g2: LineSegment StartX=16 StartY=24 StartZ=0 EndX=16 EndY=27 EndZ=0
    g3: LineSegment StartX=16 StartY=27 StartZ=0 EndX=-16 EndY=27 EndZ=0
  constraints (12):
    c: Coincident(g0,g1)
    c: Coincident(g1,g2)
    c: Coincident(g2,g3)
    c: Coincident(g3,g0)
    c: Vertical(g0)
    c: Vertical(g2)
    c: Horizontal(g1)
    c: Horizontal(g3)
    c: Distance(g-2,g2) = 16
    c: Distance(g-2,g0) = 16
    c: Distance(g-3,g3) = 1.5
    c: Distance(g-3,g1) = 1.5
FEATURE [PartDesign::Pocket] Pocket005
  BaseFeature = -> Pocket
  Direction = (0,0,1)
  Length = 11
  Length2 = 5
  Profile = -> Sketch022
  ReferenceAxis = -> Sketch022 [N_Axis]
  Refine = true
  Reversed = true
  Suppressed = false
  Type = 1
FEATURE [Sketcher::SketchObject] Sketch029
  ArcFitTolerance = 1e-06
  AttachmentSupport = -> [Pocket005]
  FullyConstrained = true
  MakeInternals = false
  MapMode = 5
  Placement = pos=(0,0,0) rot=(1,0,0;3.14159rad)
  sketch-geometry (4):
    g0: Circle CenterX=-20.3 CenterY=-23.07 CenterZ=0 NormalX=0 NormalY=0 NormalZ=1 AngleXU=0 Radius=7.5
    g1: Circle CenterX=-20.3 CenterY=-23.07 CenterZ=0 NormalX=0 NormalY=0 NormalZ=1 AngleXU=0 Radius=9.5
    g2: Circle CenterX=20.3 CenterY=-23.07 CenterZ=0 NormalX=0 NormalY=0 NormalZ=1 AngleXU=0 Radius=7.5
    g3: Circle CenterX=20.3 CenterY=-23.07 CenterZ=0 NormalX=0 NormalY=0 NormalZ=1 AngleXU=0 Radius=9.5
  constraints (8):
    c: Coincident(g0,g-3)
    c: Equal(g0,g-3)
    c: Coincident(g1,g0)
    c: Distance(g1,g0) = 2
    c: Coincident(g2,g-4)
    c: Equal(g2,g-4)
    c: Coincident(g3,g2)
    c: Distance(g3,g2) = 2
FEATURE [PartDesign::Pad] Pad019
  BaseFeature = -> Pocket005
  Direction = (0,0,-1)
  Length = 6
  Length2 = 10
  Profile = -> Sketch029
  ReferenceAxis = -> Sketch029 [N_Axis]
  Refine = true
  Suppressed = false
  Type = 0
FEATURE [Sketcher::SketchObject] Sketch030
  ArcFitTolerance = 1e-06
  AttachmentSupport = -> [Pad019]
  ExternalGeometry = -> [Pad019]
  FullyConstrained = false
  MakeInternals = false
  MapMode = 5
  Placement = pos=(0,0,-6) rot=(1,0,0;3.14159rad)
  sketch-geometry (4):
    g0: ArcOfCircle CenterX=-20.3 CenterY=-23.07 CenterZ=0 NormalX=0 NormalY=0 NormalZ=1 AngleXU=0 Radius=1.5 StartAngle=3.14159 EndAngle=6.28319
    g1: ArcOfCircle CenterX=-20.3 CenterY=-11.4402 CenterZ=0 NormalX=0 NormalY=0 NormalZ=1 AngleXU=0 Radius=1.5 StartAngle=0 EndAngle=3.14159
    g2: LineSegment StartX=-21.8 StartY=-23.07 StartZ=0 EndX=-21.8 EndY=-11.4402 EndZ=0
    g3: LineSegment StartX=-18.8 StartY=-23.07 StartZ=0 EndX=-18.8 EndY=-11.4402 EndZ=0
  constraints (8):
    c: Tangent(g0,g2) = 1.5708
    c: Tangent(g0,g3) = -1.5708
    c: Tangent(g1,g2) = 1.5708
    c: Tangent(g1,g3) = -1.5708
    c: Equal(g0,g1)
    c: Vertical(g3)
    c: Radius(g0) = 1.5
    c: Coincident(g0,g-3)
FEATURE [PartDesign::Pocket] Pocket009
  BaseFeature = -> Pad019
  Direction = (0,0,1)
  Length = 6
  Length2 = 5
  Profile = -> Sketch030
  ReferenceAxis = -> Sketch030 [N_Axis]
  Refine = true
  Suppressed = false
  Type = 0
FEATURE [PartDesign::Line] DatumLine
  AttacherType = Attacher::AttachEngineLine
  AttachmentSupport = -> [Pocket009]
  Length = 20
  MapMode = 19
  Placement = pos=(-20.3,23.07,3) rot=(0,0,1;0rad)
  ResizeMode = 0
FEATURE [PartDesign::PolarPattern] PolarPattern004
  Angle = 360
  Axis = -> DatumLine
  BaseFeature = -> Pocket009
  Mode = 0
  Occurrences = 3
  Offset = 120
  Originals = -> [Pocket009]
  Refine = true
  Suppressed = false
  TransformMode = 0
FEATURE [PartDesign::Line] DatumLine001
  AttacherType = Attacher::AttachEngineLine
  AttachmentSupport = -> [PolarPattern004]
  Length = 20
  MapMode = 19
  Placement = pos=(20.3,23.07,3) rot=(0,0,1;0rad)
  ResizeMode = 0
FEATURE [Sketcher::SketchObject] Sketch031
  ArcFitTolerance = 1e-06
  AttachmentSupport = -> [PolarPattern004]
  ExternalGeometry = -> [PolarPattern004]
  FullyConstrained = false
  MakeInternals = false
  MapMode = 5
  Placement = pos=(0,0,-6) rot=(1,0,0;3.14159rad)
  sketch-geometry (4):
    g0: ArcOfCircle CenterX=20.3 CenterY=-23.07 CenterZ=0 NormalX=0 NormalY=0 NormalZ=1 AngleXU=0 Radius=1.5 StartAngle=3.14159 EndAngle=6.28319
    g1: ArcOfCircle CenterX=20.3 CenterY=-12.6014 CenterZ=0 NormalX=0 NormalY=0 NormalZ=1 AngleXU=0 Radius=1.5 StartAngle=0 EndAngle=3.14159
    g2: LineSegment StartX=18.8 StartY=-23.07 StartZ=0 EndX=18.8 EndY=-12.6014 EndZ=0
    g3: LineSegment StartX=21.8 StartY=-23.07 StartZ=0 EndX=21.8 EndY=-12.6014 EndZ=0
  constraints (8):
    c: Tangent(g0,g2) = 1.5708
    c: Tangent(g0,g3) = -1.5708
    c: Tangent(g1,g2) = 1.5708
    c: Tangent(g1,g3) = -1.5708
    c: Equal(g0,g1)
    c: Vertical(g3)
    c: Coincident(g0,g-3)
    c: Radius(g1) = 1.5
FEATURE [PartDesign::Pocket] Pocket010
  BaseFeature = -> PolarPattern004
  Direction = (0,0,1)
  Length = 6
  Length2 = 5
  Profile = -> Sketch031
  ReferenceAxis = -> Sketch031 [N_Axis]
  Refine = true
  Suppressed = false
  Type = 0
FEATURE [PartDesign::PolarPattern] PolarPattern005
  Angle = 360
  Axis = -> DatumLine001
  BaseFeature = -> Pocket010
  Mode = 0
  Occurrences = 3
  Offset = 120
  Originals = -> [Pocket010]
  Refine = true
  Suppressed = false
  TransformMode = 0
FEATURE [Sketcher::SketchObject] Sketch033
  ArcFitTolerance = 1e-06
  AttachmentSupport = -> [PolarPattern005]
  ExternalGeometry = -> [PolarPattern005]
  FullyConstrained = false
  MakeInternals = false
  MapMode = 5
  Placement = pos=(0,0,3) rot=(0,0,1;0rad)
  sketch-geometry (16):
    g0: ArcOfCircle CenterX=-25.5 CenterY=48.3 CenterZ=0 NormalX=0 NormalY=0 NormalZ=1 AngleXU=0 Radius=6.5 StartAngle=3.14159 EndAngle=6.28319
    g1: ArcOfCircle CenterX=-25.5 CenterY=63.3 CenterZ=0 NormalX=0 NormalY=0 NormalZ=1 AngleXU=0 Radius=6.5 StartAngle=0 EndAngle=3.14159
    g2: LineSegment StartX=-32 StartY=48.3 StartZ=0 EndX=-32 EndY=63.3 EndZ=0
    g3: LineSegment StartX=-19 StartY=48.3 StartZ=0 EndX=-19 EndY=63.3 EndZ=0
    g4: ArcOfCircle CenterX=25.5 CenterY=48.3 CenterZ=0 NormalX=0 NormalY=0 NormalZ=1 AngleXU=0 Radius=6.5 StartAngle=3.14159 EndAngle=6.28319
    g5: ArcOfCircle CenterX=25.5 CenterY=63.3 CenterZ=0 NormalX=0 NormalY=0 NormalZ=1 AngleXU=0 Radius=6.5 StartAngle=2e-16 EndAngle=3.14159
    g6: LineSegment StartX=19 StartY=48.3 StartZ=0 EndX=19 EndY=63.3 EndZ=0
    g7: LineSegment StartX=32 StartY=48.3 StartZ=0 EndX=32 EndY=63.3 EndZ=0
    g8: ArcOfCircle CenterX=-25.5 CenterY=-45.5 CenterZ=0 NormalX=0 NormalY=0 NormalZ=1 AngleXU=0 Radius=6.5 StartAngle=3.14159 EndAngle=6.28319
    g9: LineSegment StartX=-19 StartY=-30.5 StartZ=0 EndX=-19 EndY=-45.5 EndZ=0
    g10: LineSegment StartX=-32 StartY=-30.5 StartZ=0 EndX=-32 EndY=-45.5 EndZ=0
    g11: ArcOfCircle CenterX=25.5 CenterY=-45.5 CenterZ=0 NormalX=0 NormalY=0 NormalZ=1 AngleXU=0 Radius=6.5 StartAngle=3.14159 EndAngle=6.28319
    g12: LineSegment StartX=32 StartY=-30.5 StartZ=0 EndX=32 EndY=-45.5 EndZ=0
    g13: LineSegment StartX=19 StartY=-30.5 StartZ=0 EndX=19 EndY=-45.5 EndZ=0
    g14: LineSegment StartX=-32 StartY=-30.5 StartZ=0 EndX=-19 EndY=-30.5 EndZ=0
    g15: LineSegment StartX=19 StartY=-30.5 StartZ=0 EndX=32 EndY=-30.5 EndZ=0
  constraints (34):
    c: Tangent(g0,g2) = 1.5708
    c: Tangent(g0,g3) = -1.5708
    c: Tangent(g1,g2) = 1.5708
    c: Tangent(g1,g3) = -1.5708
    c: Equal(g0,g1)
    c: Vertical(g3)
    c: Distance(g0,g1) = 15
    c: Vertical(g0,g-3)
    c: Radius(g0) = 6.5
    c: Tangent(g4,g6) = 1.5708
    c: Tangent(g4,g7) = -1.5708
    c: Tangent(g5,g6) = 1.5708
    c: Tangent(g5,g7) = -1.5708
    c: Equal(g4,g5)
    c: Vertical(g7)
    c: Distance(g4,g5) = 15
    c: Radius(g4) = 6.5
    c: Vertical(g4,g-4)
    c: Horizontal(g0,g4)
    c: DistanceY(g-1,g0) = 48.3
    c: Tangent(g8,g9) = 1.5708
    c: Tangent(g8,g10) = -1.5708
    c: Vertical(g10)
    c: Vertical(g10,g-3)
    c: Tangent(g11,g12) = 1.5708
    c: Tangent(g11,g13) = -1.5708
    c: Vertical(g13)
    c: Vertical(g12,g-4)
    c: Coincident(g10,g14)
    c: Coincident(g14,g9)
    c: Horizontal(g14)
    c: Coincident(g15,g13)
    c: Coincident(g15,g12)
    c: Horizontal(g15)
FEATURE [PartDesign::Pad] Pad021
  BaseFeature = -> PolarPattern005
  Direction = (0,0,1)
  Length = 14
  Length2 = 10
  Profile = -> Sketch033
  ReferenceAxis = -> Sketch033 [N_Axis]
  Refine = true
  Reversed = true
  Suppressed = false
  Type = 0
FEATURE [Sketcher::SketchObject] Sketch034
  ArcFitTolerance = 1e-06
  AttachmentSupport = -> [Pad021]
  ExternalGeometry = -> [Pad021]
  FullyConstrained = false
  MakeInternals = false
  MapMode = 5
  Placement = pos=(0,0,3) rot=(0,0,1;0rad)
  sketch-geometry (8):
    g0: LineSegment StartX=-58.6623 StartY=87.6289 StartZ=0 EndX=-58.6623 EndY=-72.0446 EndZ=0
    g1: LineSegment StartX=-58.6623 StartY=-72.0446 StartZ=0 EndX=67.0121 EndY=-72.0446 EndZ=0
    g2: LineSegment StartX=67.0121 StartY=-72.0446 StartZ=0 EndX=67.0121 EndY=87.6289 EndZ=0
    g3: LineSegment StartX=67.0121 StartY=87.6289 StartZ=0 EndX=-58.6623 EndY=87.6289 EndZ=0
    g4: LineSegment StartX=-32 StartY=57 StartZ=0 EndX=-32 EndY=-40 EndZ=0
    g5: LineSegment StartX=-32 StartY=-40 StartZ=0 EndX=32 EndY=-40 EndZ=0
    g6: LineSegment StartX=32 StartY=-40 StartZ=0 EndX=32 EndY=57 EndZ=0
    g7: LineSegment StartX=32 StartY=57 StartZ=0 EndX=-32 EndY=57 EndZ=0
  constraints (19):
    c: Coincident(g0,g1)
    c: Coincident(g1,g2)
    c: Coincident(g2,g3)
    c: Coincident(g3,g0)
    c: Vertical(g0)
    c: Vertical(g2)
    c: Horizontal(g1)
    c: Horizontal(g3)
    c: Coincident(g4,g5)
    c: Coincident(g5,g6)
    c: Coincident(g6,g7)
    c: Coincident(g7,g4)
    c: Vertical(g4)
    c: Vertical(g6)
    c: Horizontal(g5)
    c: Horizontal(g7)
    c: Horizontal(g4,g-3)
    c: Vertical(g4,g-5)
    c: Coincident(g5,g-6)
FEATURE [PartDesign::Pocket] Pocket013
  BaseFeature = -> Pad021
  Direction = (0,0,-1)
  Length = 3
  Length2 = 5
  Profile = -> Sketch034
  ReferenceAxis = -> Sketch034 [N_Axis]
  Refine = true
  Suppressed = false
  Type = 0
FEATURE [Sketcher::SketchObject] Sketch
  ArcFitTolerance = 1e-06
  AttachmentSupport = -> [Pocket013]
  FullyConstrained = true
  MakeInternals = false
  MapMode = 5
  Placement = pos=(0,0,-11) rot=(1,0,0;3.14159rad)
  sketch-geometry (10):
    g0: LineSegment StartX=-31 StartY=31 StartZ=0 EndX=-31 EndY=-49 EndZ=0
    g1: LineSegment StartX=-26 StartY=-54 StartZ=0 EndX=26 EndY=-54 EndZ=0
    g2: LineSegment StartX=31 StartY=-49 StartZ=0 EndX=31 EndY=31 EndZ=0
    g3: LineSegment StartX=26 StartY=36 StartZ=0 EndX=-26 EndY=36 EndZ=0
    g4: ArcOfCircle CenterX=-26 CenterY=31 CenterZ=0 NormalX=0 NormalY=0 NormalZ=1 AngleXU=0 Radius=5 StartAngle=1.5708 EndAngle=3.14159
    g5: ArcOfCircle CenterX=-26 CenterY=-49 CenterZ=0 NormalX=0 NormalY=0 NormalZ=1 AngleXU=0 Radius=5 StartAngle=3.14159 EndAngle=4.71239
    g6: ArcOfCircle CenterX=26 CenterY=-49 CenterZ=0 NormalX=0 NormalY=0 NormalZ=1 AngleXU=0 Radius=5 StartAngle=4.71239 EndAngle=6.28319
    g7: ArcOfCircle CenterX=26 CenterY=31 CenterZ=0 NormalX=0 NormalY=0 NormalZ=1 AngleXU=0 Radius=5 StartAngle=0 EndAngle=1.5708
    g8: GeomPoint [constr] X=-31 Y=36 Z=0
    g9: GeomPoint [constr] X=31 Y=-54 Z=0
  constraints (24):
    c: Tangent(g0,g4) = -1.5708
    c: Tangent(g0,g5) = -1.5708
    c: Tangent(g1,g5) = -1.5708
    c: Tangent(g1,g6) = -1.5708
    c: Tangent(g2,g6) = -1.5708
    c: Tangent(g2,g7) = -1.5708
    c: Tangent(g3,g7) = -1.5708
    c: Tangent(g3,g4) = -1.5708
    c: Vertical(g0)
    c: Vertical(g2)
    c: Horizontal(g1)
    c: Horizontal(g3)
    c: Equal(g4,g5)
    c: Equal(g5,g6)
    c: Equal(g6,g7)
    c: PointOnObject(g8,g0)
    c: PointOnObject(g8,g3)
    c: PointOnObject(g9,g1)
    c: PointOnObject(g9,g2)
    c: Distance(g0,g2) = 62
    c: Distance(g1,g3) = 90
    c: Radius(g5) = 5
    c: DistanceY(g-1,g7) = 31
    c: Distance(g2,g-2) = 31
FEATURE [PartDesign::Pocket] Pocket019
  BaseFeature = -> Pocket013
  Direction = (0,0,1)
  Length = 1.5
  Length2 = 5
  Profile = -> Sketch
  ReferenceAxis = -> Sketch [N_Axis]
  Refine = true
  Suppressed = false
  Type = 0
FEATURE [Sketcher::SketchObject] Sketch042
  ArcFitTolerance = 1e-06
  AttachmentSupport = -> [Pocket019]
  ExternalGeometry = -> [Pocket019]
  FullyConstrained = true
  MakeInternals = false
  MapMode = 5
  Placement = pos=(0,0,-11) rot=(1,0,0;3.14159rad)
  sketch-geometry (8):
    g0: Circle CenterX=-25.4 CenterY=30.5 CenterZ=0 NormalX=0 NormalY=0 NormalZ=1 AngleXU=0 Radius=1.5
    g1: Circle CenterX=25.4 CenterY=30.5 CenterZ=0 NormalX=0 NormalY=0 NormalZ=1 AngleXU=0 Radius=1.5
    g2: Circle CenterX=25.5 CenterY=-48.3 CenterZ=0 NormalX=0 NormalY=0 NormalZ=1 AngleXU=0 Radius=1.5
    g3: Circle CenterX=-25.5 CenterY=-48.3 CenterZ=0 NormalX=0 NormalY=0 NormalZ=1 AngleXU=0 Radius=1.5
    g4: Circle CenterX=-25.5 CenterY=45.5 CenterZ=0 NormalX=0 NormalY=0 NormalZ=1 AngleXU=0 Radius=1.5
    g5: Circle CenterX=25.5 CenterY=45.5 CenterZ=0 NormalX=0 NormalY=0 NormalZ=1 AngleXU=0 Radius=1.5
    g6: Circle CenterX=25.5 CenterY=-63.3 CenterZ=0 NormalX=0 NormalY=0 NormalZ=1 AngleXU=0 Radius=1.5
    g7: Circle CenterX=-25.5 CenterY=-63.3 CenterZ=0 NormalX=0 NormalY=0 NormalZ=1 AngleXU=0 Radius=1.5
  constraints (16):
    c: Diameter(g0) = 3
    c: Coincident(g0,g-3)
    c: Diameter(g1) = 3
    c: Coincident(g1,g-4)
    c: Diameter(g2) = 3
    c: Coincident(g2,g-6)
    c: Diameter(g3) = 3
    c: Coincident(g3,g-5)
    c: Diameter(g4) = 3
    c: Coincident(g4,g-7)
    c: Diameter(g5) = 3
    c: Coincident(g5,g-8)
    c: Diameter(g6) = 3
    c: Coincident(g6,g-9)
    c: Diameter(g7) = 3
    c: Coincident(g7,g-10)
FEATURE [PartDesign::Pocket] Pocket020
  BaseFeature = -> Pocket019
  Direction = (0,0,1)
  Length = 11
  Length2 = 5
  Profile = -> Sketch042
  ReferenceAxis = -> Sketch042 [N_Axis]
  Refine = true
  Suppressed = false
  Type = 0
FEATURE [PartDesign::Chamfer] Chamfer008
  Angle = 45
  Base = -> Pocket020 [Edge18]
  BaseFeature = -> Pocket020
  ChamferType = 0
  FlipDirection = false
  Refine = true
  Size = 8
  Size2 = 1
  SupportTransform = false
  Suppressed = false
  UseAllEdges = false
FEATURE [PartDesign::Chamfer] Chamfer009
  Angle = 45
  Base = -> Chamfer008 [Edge5]
  BaseFeature = -> Chamfer008
  ChamferType = 0
  FlipDirection = false
  Refine = true
  Size = 8
  Size2 = 1
  SupportTransform = false
  Suppressed = false
  UseAllEdges = false
FEATURE [PartDesign::Chamfer] Chamfer010
  Angle = 45
  Base = -> Chamfer009 [Edge9,Edge13,Edge11]
  BaseFeature = -> Chamfer009
  ChamferType = 0
  FlipDirection = false
  Refine = true
  Size = 3
  Size2 = 1
  SupportTransform = false
  Suppressed = false
  UseAllEdges = false
FEATURE [PartDesign::Chamfer] Chamfer011
  Angle = 45
  Base = -> Chamfer010 [Edge16,Edge17,Edge15]
  BaseFeature = -> Chamfer010
  ChamferType = 0
  FlipDirection = false
  Refine = true
  Size = 3
  Size2 = 1
  SupportTransform = false
  Suppressed = false
  UseAllEdges = false
FEATURE [PartDesign::Body] Body001  label="NavBoardTop"
  AllowCompound = false
  Group = -> [Sketch001,Pad001,Sketch012,Pad011,Sketch019,Pocket003,PolarPattern,Sketch020,Pad016,Sketch002,Pocket,Sketch022,Pocket005,Sketch029,Pad019,Sketch030,Pocket009,DatumLine,PolarPattern004,DatumLine001,Sketch031,Pocket010,PolarPattern005,Sketch033,Pad021,Sketch034,Pocket013,Sketch,Pocket019,Sketch042,Pocket020,Chamfer008,Chamfer009,Chamfer010,Chamfer011]
  Origin = -> Origin002
  Placement = pos=(0,0,12) rot=(0,0,1;0rad)
  Tip = -> Chamfer011
COMPONENT P2 — recipe-attached ("BtnEsc", modeled in this document).
Construction recipe (the document's own serialized feature program — sketch geometry with constraints, then the solid features built on it; lengths are millimeters unless a unit is written):

FEATURE [Sketcher::SketchObject] Sketch004
  ArcFitTolerance = 1e-06
  AttachmentSupport = -> [XY_Plane004]
  FullyConstrained = true
  MakeInternals = false
  MapMode = 5
  sketch-geometry (1):
    g0: Circle CenterX=0 CenterY=0 CenterZ=0 NormalX=0 NormalY=0 NormalZ=1 AngleXU=0 Radius=7.25
  constraints (2):
    c: Diameter(g0) = 14.5
    c: Coincident(g0,g-1)
FEATURE [PartDesign::Pad] Pad003
  Direction = (0,0,1)
  Length = 11
  Length2 = 10
  Profile = -> Sketch004
  ReferenceAxis = -> Sketch004 [N_Axis]
  Refine = true
  Suppressed = false
  Type = 0
FEATURE [PartDesign::Chamfer] Chamfer002
  Angle = 45
  Base = -> Pad003 [Edge3]
  BaseFeature = -> Pad003
  ChamferType = 0
  FlipDirection = false
  Refine = true
  Size = 1
  Size2 = 1
  SupportTransform = false
  Suppressed = false
  UseAllEdges = false
FEATURE [Sketcher::SketchObject] Sketch035
  ArcFitTolerance = 1e-06
  AttachmentSupport = -> [Chamfer002]
  FullyConstrained = false
  MakeInternals = false
  MapMode = 5
  Placement = pos=(0,0,11) rot=(0,0,1;0rad)
  sketch-geometry (11):
    g0: LineSegment StartX=-0.858818 StartY=4.92477 StartZ=0 EndX=-3.85882 EndY=1.92477 EndZ=0
    g1: LineSegment StartX=-3.85882 StartY=1.92477 StartZ=0 EndX=-0.858818 EndY=-1.07523 EndZ=0
    g2: LineSegment StartX=-0.858818 StartY=-1.07523 StartZ=0 EndX=-0.858818 EndY=0.924774 EndZ=0
    g3: LineSegment StartX=-0.858818 StartY=0.924774 StartZ=0 EndX=0.385732 EndY=0.924774 EndZ=0
    g4: LineSegment StartX=-0.858818 StartY=4.92477 StartZ=0 EndX=-0.858818 EndY=2.92477 EndZ=0
    g5: LineSegment StartX=-0.858818 StartY=2.92477 StartZ=0 EndX=0.385732 EndY=2.92477 EndZ=0
    g6: ArcOfCircle CenterX=0.385732 CenterY=-0.648527 CenterZ=0 NormalX=0 NormalY=0 NormalZ=1 AngleXU=0 Radius=1.5733 StartAngle=4.71239 EndAngle=7.85398
    g7: ArcOfCircle CenterX=0.385732 CenterY=-0.648527 CenterZ=0 NormalX=0 NormalY=0 NormalZ=1 AngleXU=0 Radius=3.5733 StartAngle=4.71239 EndAngle=7.85398
    g8: LineSegment StartX=0.385731 StartY=-2.22183 StartZ=0 EndX=-1.24855 EndY=-2.22183 EndZ=0
    g9: LineSegment StartX=-1.24855 StartY=-2.22183 StartZ=0 EndX=-1.24855 EndY=-4.22183 EndZ=0
    g10: LineSegment StartX=-1.24855 StartY=-4.22183 StartZ=0 EndX=0.38573 EndY=-4.22183 EndZ=0
  constraints (26):
    c: Coincident(g0,g1)
    c: Coincident(g1,g2)
    c: Coincident(g2,g3)
    c: Horizontal(g3)
    c: Coincident(g0,g4)
    c: Coincident(g4,g5)
    c: Horizontal(g5)
    c: Vertical(g4)
    c: Vertical(g2)
    c: Vertical(g4,g2)
    c: Distance(g4,g4) = 2
    c: DistanceY(g2,g2) = 2
    c: Distance(g3,g5) = 2
    c: Angle(g1,g0) = 1.5708
    c: DistanceY(g0,g4) = 1
    c: Coincident(g6,g3)
    c: Vertical(g6,g3)
    c: Vertical(g5,g3)
    c: Coincident(g7,g6)
    c: Coincident(g7,g5)
    c: Tangent(g6,g8) = 1.5708
    c: Coincident(g8,g9)
    c: Vertical(g9)
    c: Coincident(g9,g10)
    c: Coincident(g10,g7)
    c: Horizontal(g10)
FEATURE [Sketcher::SketchObject] Sketch036
  ArcFitTolerance = 1e-06
  AttachmentOffset = pos=(0,0,-6.5) rot=(0,0,1;0rad)
  AttachmentSupport = -> [Chamfer002]
  ExternalGeometry = -> [Chamfer002]
  FullyConstrained = true
  MakeInternals = false
  MapMode = 5
  Placement = pos=(0,0,6.5) rot=(1,0,0;3.14159rad)
  sketch-geometry (4):
    g0: ArcOfCircle CenterX=0 CenterY=0 CenterZ=0 NormalX=0 NormalY=0 NormalZ=1 AngleXU=0 Radius=7.25 StartAngle=1.40451 EndAngle=1.73708
    g1: LineSegment StartX=-1.2 StartY=7.15 StartZ=0 EndX=-1.2 EndY=9.45 EndZ=0
    g2: LineSegment StartX=-1.2 StartY=9.45 StartZ=0 EndX=1.2 EndY=9.45 EndZ=0
    g3: LineSegment StartX=1.2 StartY=9.45 StartZ=0 EndX=1.2 EndY=7.15 EndZ=0
  constraints (12):
    c: Coincident(g0,g-1)
    c: PointOnObject(g0,g-3)
    c: Coincident(g0,g1)
    c: Coincident(g1,g2)
    c: Horizontal(g2)
    c: Coincident(g2,g3)
    c: Coincident(g3,g0)
    c: Vertical(g3)
    c: Vertical(g1)
    c: Distance(g-2,g1) = 1.2
    c: Distance(g-2,g3) = 1.2
    c: DistanceY(g3,g3) = 2.3
FEATURE [PartDesign::Pad] Pad022
  BaseFeature = -> Chamfer002
  Direction = (0,0,-1)
  Length = 2.5
  Length2 = 10
  Profile = -> Sketch036
  ReferenceAxis = -> Sketch036 [N_Axis]
  Refine = true
  Suppressed = false
  Type = 0
FEATURE [PartDesign::PolarPattern] PolarPattern007
  Angle = 360
  Axis = -> Sketch036 [N_Axis]
  BaseFeature = -> Pad022
  Mode = 0
  Occurrences = 3
  Offset = 120
  Originals = -> [Pad022]
  Refine = true
  Suppressed = false
  TransformMode = 0
FEATURE [PartDesign::Pocket] Pocket014
  BaseFeature = -> PolarPattern007
  Direction = (0,0,-1)
  Length = 1
  Length2 = 5
  Profile = -> Sketch035
  ReferenceAxis = -> Sketch035 [N_Axis]
  Refine = true
  Suppressed = false
  Type = 0
FEATURE [Sketcher::SketchObject] Sketch040
  ArcFitTolerance = 1e-06
  AttachmentSupport = -> [Pocket014]
  FullyConstrained = true
  MakeInternals = false
  MapMode = 5
  Placement = pos=(0,0,0) rot=(1,0,0;3.14159rad)
  sketch-geometry (10):
    g0: LineSegment StartX=-4 StartY=2.5 StartZ=0 EndX=-4 EndY=-2.5 EndZ=0
    g1: LineSegment StartX=-2.5 StartY=-4 StartZ=0 EndX=2.5 EndY=-4 EndZ=0
    g2: LineSegment StartX=4 StartY=-2.5 StartZ=0 EndX=4 EndY=2.5 EndZ=0
    g3: LineSegment StartX=2.5 StartY=4 StartZ=0 EndX=-2.5 EndY=4 EndZ=0
    g4: ArcOfCircle CenterX=-2.5 CenterY=2.5 CenterZ=0 NormalX=0 NormalY=0 NormalZ=1 AngleXU=0 Radius=1.5 StartAngle=1.5708 EndAngle=3.14159
    g5: ArcOfCircle CenterX=-2.5 CenterY=-2.5 CenterZ=0 NormalX=0 NormalY=0 NormalZ=1 AngleXU=0 Radius=1.5 StartAngle=3.14159 EndAngle=4.71239
    g6: ArcOfCircle CenterX=2.5 CenterY=-2.5 CenterZ=0 NormalX=0 NormalY=0 NormalZ=1 AngleXU=0 Radius=1.5 StartAngle=4.71239 EndAngle=6.28319
    g7: ArcOfCircle CenterX=2.5 CenterY=2.5 CenterZ=0 NormalX=0 NormalY=0 NormalZ=1 AngleXU=0 Radius=1.5 StartAngle=0 EndAngle=1.5708
    g8: GeomPoint [constr] X=-4 Y=4 Z=0
    g9: GeomPoint [constr] X=4 Y=-4 Z=0
  constraints (23):
    c: Tangent(g0,g4) = -1.5708
    c: Tangent(g0,g5) = -1.5708
    c: Tangent(g1,g5) = -1.5708
    c: Tangent(g1,g6) = -1.5708
    c: Tangent(g2,g6) = -1.5708
    c: Tangent(g2,g7) = -1.5708
    c: Tangent(g3,g7) = -1.5708
    c: Tangent(g3,g4) = -1.5708
    c: Vertical(g0)
    c: Vertical(g2)
    c: Horizontal(g1)
    c: Horizontal(g3)
    c: Equal(g4,g5)
    c: Equal(g5,g6)
    c: Equal(g6,g7)
    c: PointOnObject(g8,g0)
    c: PointOnObject(g8,g3)
    c: PointOnObject(g9,g1)
    c: PointOnObject(g9,g2)
    c: Radius(g5) = 1.5
    c: DistanceX(g-1,g9) = 4
    c: DistanceY(g9,g-1) = 4
    c: Symmetric(g9,g8,g-1)
FEATURE [PartDesign::Pocket] Pocket017
  BaseFeature = -> Pocket014
  Direction = (0,0,1)
  Length = 1.5
  Length2 = 5
  Profile = -> Sketch040
  ReferenceAxis = -> Sketch040 [N_Axis]
  Refine = true
  Suppressed = false
  Type = 0
FEATURE [PartDesign::Body] Body002  label="BtnEsc"
  AllowCompound = false
  Group = -> [Sketch004,Pad003,Chamfer002,Sketch035,Sketch036,Pad022,PolarPattern007,Pocket014,Sketch040,Pocket017]
  Origin = -> Origin004
  Placement = pos=(-20.3,23.1,10) rot=(0,0,1;0rad)
  Tip = -> Pocket017
COMPONENT P3 — recipe-attached ("BtnOk", modeled in this document).
Construction recipe (the document's own serialized feature program — sketch geometry with constraints, then the solid features built on it; lengths are millimeters unless a unit is written):

FEATURE [Sketcher::SketchObject] Sketch006
  ArcFitTolerance = 1e-06
  AttachmentSupport = -> [XY_Plane005]
  FullyConstrained = true
  MakeInternals = false
  MapMode = 5
  sketch-geometry (1):
    g0: Circle CenterX=0 CenterY=0 CenterZ=0 NormalX=0 NormalY=0 NormalZ=1 AngleXU=0 Radius=7.25
  constraints (2):
    c: Diameter(g0) = 14.5
    c: Coincident(g0,g-1)
FEATURE [PartDesign::Pad] Pad005
  Direction = (0,0,1)
  Length = 11
  Length2 = 10
  Profile = -> Sketch006
  ReferenceAxis = -> Sketch006 [N_Axis]
  Refine = true
  Suppressed = false
  Type = 0
FEATURE [Sketcher::SketchObject] Sketch025
  ArcFitTolerance = 1e-06
  AttachmentSupport = -> [Pad005]
  FullyConstrained = true
  MakeInternals = false
  MapMode = 5
  Placement = pos=(0,0,0) rot=(1,0,0;3.14159rad)
  sketch-geometry (1):
    g0: Circle CenterX=0 CenterY=0 CenterZ=0 NormalX=0 NormalY=0 NormalZ=1 AngleXU=0 Radius=6
  constraints (2):
    c: Diameter(g0) = 12
    c: Coincident(g0,g-1)
FEATURE [PartDesign::Pocket] Pocket006
  BaseFeature = -> Pad005
  Direction = (0,0,1)
  Length = 2
  Length2 = 5
  Profile = -> Sketch025
  ReferenceAxis = -> Sketch025 [N_Axis]
  Refine = true
  Suppressed = false
  Type = 0
FEATURE [Part::Part2DObjectPython] ShapeString  # Draft 2D object (typed FeaturePython)
  FontFile = <path>
  Fuse = false
  Justification = 6
  JustificationReference = 0
  KeepLeftMargin = false
  MakeFace = true
  ObliqueAngle = 0
  Placement = pos=(-5,-2.5,11) rot=(0,0,1;0rad)
  ScaleToSize = true
  Size = 5
  String = OK
  Tracking = 0
FEATURE [PartDesign::Pocket] Pocket012
  BaseFeature = -> Pocket006
  Direction = (0,0,-1)
  Length = 1
  Length2 = 5
  Profile = -> ShapeString
  ReferenceAxis = -> ShapeString [N_Axis]
  Refine = true
  Suppressed = false
  Type = 0
FEATURE [PartDesign::Chamfer] Chamfer006
  Angle = 45
  Base = -> Pocket012 [Edge3]
  BaseFeature = -> Pocket012
  ChamferType = 0
  FlipDirection = false
  Refine = true
  Size = 1
  Size2 = 1
  SupportTransform = false
  Suppressed = false
  UseAllEdges = false
FEATURE [Sketcher::SketchObject] Sketch043
  ArcFitTolerance = 1e-06
  AttachmentOffset = pos=(0,0,-5) rot=(0,0,1;0rad)
  AttachmentSupport = -> [Chamfer006]
  ExternalGeometry = -> [Chamfer006]
  FullyConstrained = false
  MakeInternals = false
  MapMode = 5
  Placement = pos=(0,0,5) rot=(1,0,0;3.14159rad)
  sketch-geometry (4):
    g0: LineSegment StartX=-1 StartY=9.1807 StartZ=0 EndX=-1 EndY=7.1807 EndZ=0
    g1: LineSegment StartX=1 StartY=9.1807 StartZ=0 EndX=1 EndY=7.1807 EndZ=0
    g2: ArcOfCircle CenterX=0 CenterY=0 CenterZ=0 NormalX=0 NormalY=0 NormalZ=1 AngleXU=0 Radius=7.25 StartAngle=1.43242 EndAngle=1.70917
    g3: ArcOfCircle CenterX=0 CenterY=0 CenterZ=0 NormalX=0 NormalY=0 NormalZ=1 AngleXU=0 Radius=9.235 StartAngle=1.4623 EndAngle=1.67929
  constraints (13):
    c: Vertical(g0)
    c: Distance(g-2,g0) = 1
    c: Vertical(g1)
    c: Distance(g-2,g1) = 1
    c: Coincident(g2,g-1)
    c: PointOnObject(g2,g-3)
    c: PointOnObject(g0,g2)
    c: PointOnObject(g1,g-3)
    c: Coincident(g3,g2)
    c: Coincident(g3,g1)
    c: Coincident(g3,g0)
    c: Vertical(g2,g1)
    c: DistanceY(g1,g1) = 2
FEATURE [PartDesign::Pad] Pad
  BaseFeature = -> Chamfer006
  Direction = (0,0,-1)
  Length = 2
  Length2 = 10
  Profile = -> Sketch043
  ReferenceAxis = -> Sketch043 [N_Axis]
  Refine = true
  Reversed = true
  Suppressed = false
  Type = 0
FEATURE [PartDesign::PolarPattern] PolarPattern009
  Angle = 360
  Axis = -> Sketch043 [N_Axis]
  BaseFeature = -> Pad
  Mode = 0
  Occurrences = 3
  Offset = 120
  Originals = -> [Pad]
  Refine = true
  Suppressed = false
  TransformMode = 0
FEATURE [PartDesign::Body] Body003  label="BtnOk"
  AllowCompound = false
  Group = -> [Sketch006,Pad005,Sketch025,Pocket006,ShapeString,Pocket012,Chamfer006,Sketch043,Pad,PolarPattern009]
  Origin = -> Origin005
  Placement = pos=(0,0,10) rot=(0,0,1;0rad)
  Tip = -> PolarPattern009
COMPONENT P4 — recipe-attached ("BtnGo", modeled in this document).
Construction recipe (the document's own serialized feature program — sketch geometry with constraints, then the solid features built on it; lengths are millimeters unless a unit is written):

FEATURE [Sketcher::SketchObject] Sketch016
  ArcFitTolerance = 1e-06
  AttachmentSupport = -> [XY_Plane008]
  FullyConstrained = true
  MakeInternals = false
  MapMode = 5
  sketch-geometry (4):
    g0: ArcOfCircle CenterX=-4 CenterY=0 CenterZ=0 NormalX=0 NormalY=0 NormalZ=1 AngleXU=0 Radius=7.5 StartAngle=1.5708 EndAngle=4.71239
    g1: ArcOfCircle CenterX=4 CenterY=2e-16 CenterZ=0 NormalX=0 NormalY=0 NormalZ=1 AngleXU=0 Radius=7.5 StartAngle=4.71239 EndAngle=7.85398
    g2: LineSegment StartX=-4 StartY=7.5 StartZ=0 EndX=4 EndY=7.5 EndZ=0
    g3: LineSegment StartX=-4 StartY=-7.5 StartZ=0 EndX=4 EndY=-7.5 EndZ=0
  constraints (10):
    c: Tangent(g0,g2) = 1.5708
    c: Tangent(g0,g3) = -1.5708
    c: Tangent(g1,g2) = 1.5708
    c: Tangent(g1,g3) = -1.5708
    c: Equal(g0,g1)
    c: Horizontal(g3)
    c: Distance(g0,g1) = 8
    c: Radius(g0) = 7.5
    c: PointOnObject(g0,g-1)
    c: DistanceX(g0,g-1) = 4
FEATURE [PartDesign::Pad] Pad013
  Direction = (0,0,1)
  Length = 11.5
  Length2 = 10
  Profile = -> Sketch016
  ReferenceAxis = -> Sketch016 [N_Axis]
  Refine = true
  Suppressed = false
  Type = 0
FEATURE [Sketcher::SketchObject] Sketch023
  ArcFitTolerance = 1e-06
  AttachmentSupport = -> [XZ_Plane008]
  ExternalGeometry = -> [Pad013]
  FullyConstrained = true
  MakeInternals = false
  MapMode = 5
  Placement = pos=(0,0,0) rot=(1,0,0;1.5708rad)
  sketch-geometry (4):
    g0: LineSegment StartX=-4 StartY=7 StartZ=0 EndX=-4 EndY=5 EndZ=0
    g1: LineSegment StartX=-14.5 StartY=5 StartZ=0 EndX=-4 EndY=5 EndZ=0
    g2: LineSegment StartX=-14.5 StartY=7 StartZ=0 EndX=-4 EndY=7 EndZ=0
    g3: LineSegment StartX=-14.5 StartY=7 StartZ=0 EndX=-14.5 EndY=5 EndZ=0
  constraints (12):
    c: Vertical(g0)
    c: Coincident(g1,g0)
    c: Horizontal(g1)
    c: Horizontal(g2)
    c: Distance(g-3,g2) = 4.5
    c: Coincident(g0,g2)
    c: Coincident(g3,g2)
    c: Coincident(g3,g1)
    c: Vertical(g3)
    c: Distance(g0,g3) = 10.5
    c: Distance(g3,g3) = 2
    c: Vertical(g0,g-3)
FEATURE [PartDesign::Pad] Pad017
  BaseFeature = -> Pad013
  Direction = (0,-1,2e-16)
  Length = 2.5
  Length2 = 10
  Midplane = true
  Profile = -> Sketch023
  ReferenceAxis = -> Sketch023 [N_Axis]
  Refine = true
  Suppressed = false
  Type = 0
FEATURE [PartDesign::Mirrored] Mirrored
  BaseFeature = -> Pad017
  MirrorPlane = -> Sketch023 [V_Axis]
  Originals = -> [Pad017]
  Refine = true
  Suppressed = false
  TransformMode = 0
FEATURE [Part::Part2DObjectPython] ShapeString001  # Draft 2D object (typed FeaturePython)
  FontFile = <path>
  Fuse = false
  Justification = 6
  JustificationReference = 0
  KeepLeftMargin = false
  MakeFace = true
  ObliqueAngle = 0
  Placement = pos=(-8,-4,11.5) rot=(0,0,1;0rad)
  ScaleToSize = true
  Size = 8
  String = GO
  Tracking = 0
FEATURE [PartDesign::Pocket] Pocket016
  BaseFeature = -> Mirrored
  Direction = (0,0,-1)
  Length = 1
  Length2 = 5
  Profile = -> ShapeString001
  ReferenceAxis = -> ShapeString001 [N_Axis]
  Refine = true
  Suppressed = false
  Type = 0
FEATURE [PartDesign::Chamfer] Chamfer007
  Angle = 45
  Base = -> Pocket016 [Edge15]
  BaseFeature = -> Pocket016
  ChamferType = 0
  FlipDirection = false
  Refine = true
  Size = 1
  Size2 = 1
  SupportTransform = false
  Suppressed = false
  UseAllEdges = false
FEATURE [Sketcher::SketchObject] Sketch045
  ArcFitTolerance = 1e-06
  AttachmentSupport = -> [Chamfer007]
  FullyConstrained = true
  MakeInternals = false
  MapMode = 5
  Placement = pos=(0,0,0) rot=(1,0,0;3.14159rad)
  sketch-geometry (10):
    g0: LineSegment StartX=-4 StartY=2 StartZ=0 EndX=-4 EndY=-2 EndZ=0
    g1: LineSegment StartX=-2 StartY=-4 StartZ=0 EndX=2 EndY=-4 EndZ=0
    g2: LineSegment StartX=4 StartY=-2 StartZ=0 EndX=4 EndY=2 EndZ=0
    g3: LineSegment StartX=2 StartY=4 StartZ=0 EndX=-2 EndY=4 EndZ=0
    g4: ArcOfCircle CenterX=-2 CenterY=2 CenterZ=0 NormalX=0 NormalY=0 NormalZ=1 AngleXU=0 Radius=2 StartAngle=1.5708 EndAngle=3.14159
    g5: ArcOfCircle CenterX=-2 CenterY=-2 CenterZ=0 NormalX=0 NormalY=0 NormalZ=1 AngleXU=0 Radius=2 StartAngle=3.14159 EndAngle=4.71239
    g6: ArcOfCircle CenterX=2 CenterY=-2 CenterZ=0 NormalX=0 NormalY=0 NormalZ=1 AngleXU=0 Radius=2 StartAngle=4.71239 EndAngle=6.28319
    g7: ArcOfCircle CenterX=2 CenterY=2 CenterZ=0 NormalX=0 NormalY=0 NormalZ=1 AngleXU=0 Radius=2 StartAngle=0 EndAngle=1.5708
    g8: GeomPoint [constr] X=-4 Y=4 Z=0
    g9: GeomPoint [constr] X=4 Y=-4 Z=0
  constraints (23):
    c: Tangent(g0,g4) = -1.5708
    c: Tangent(g0,g5) = -1.5708
    c: Tangent(g1,g5) = -1.5708
    c: Tangent(g1,g6) = -1.5708
    c: Tangent(g2,g6) = -1.5708
    c: Tangent(g2,g7) = -1.5708
    c: Tangent(g3,g7) = -1.5708
    c: Tangent(g3,g4) = -1.5708
    c: Vertical(g0)
    c: Vertical(g2)
    c: Horizontal(g1)
    c: Horizontal(g3)
    c: Equal(g4,g5)
    c: Equal(g5,g6)
    c: Equal(g6,g7)
    c: PointOnObject(g8,g0)
    c: PointOnObject(g8,g3)
    c: PointOnObject(g9,g1)
    c: PointOnObject(g9,g2)
    c: Distance(g0,g2) = 8
    c: Distance(g1,g3) = 8
    c: Radius(g5) = 2
    c: Symmetric(g4,g6,g-1)
FEATURE [PartDesign::Pocket] Pocket022
  BaseFeature = -> Chamfer007
  Direction = (0,0,1)
  Length = 2
  Length2 = 5
  Profile = -> Sketch045
  ReferenceAxis = -> Sketch045 [N_Axis]
  Refine = true
  Suppressed = false
  Type = 0
FEATURE [PartDesign::Body] Body006  label="BtnGo"
  AllowCompound = false
  Group = -> [Sketch016,Pad013,Sketch023,Pad017,Mirrored,ShapeString001,Pocket016,Chamfer007,Sketch045,Pocket022]
  Origin = -> Origin008
  Placement = pos=(0,-25.5,9.5) rot=(0,0,1;0rad)
  Tip = -> Pocket022
COMPONENT P5 — recipe-attached ("Btn4Direction", modeled in this document).
Construction recipe (the document's own serialized feature program — sketch geometry with constraints, then the solid features built on it; lengths are millimeters unless a unit is written):

FEATURE [Sketcher::SketchObject] Sketch024
  ArcFitTolerance = 1e-06
  AttachmentSupport = -> [YZ_Plane009]
  FullyConstrained = true
  MakeInternals = false
  MapMode = 5
  Placement = pos=(0,0,0) rot=(0.57735,0.57735,0.57735;2.0944rad)
  sketch-geometry (4):
    g0: LineSegment StartX=7.5 StartY=-1.5 StartZ=0 EndX=16 EndY=-1.5 EndZ=0
    g1: LineSegment StartX=16 StartY=-1.5 StartZ=0 EndX=16 EndY=9.5 EndZ=0
    g2: LineSegment StartX=16 StartY=9.5 StartZ=0 EndX=7.5 EndY=9.5 EndZ=0
    g3: LineSegment StartX=7.5 StartY=9.5 StartZ=0 EndX=7.5 EndY=-1.5 EndZ=0
  constraints (12):
    c: Coincident(g0,g1)
    c: Vertical(g1)
    c: Coincident(g1,g2)
    c: Horizontal(g2)
    c: Coincident(g2,g3)
    c: Vertical(g3)
    c: Distance(g-2,g3) = 7.5
    c: Distance(g-1,g0) = 1.5
    c: Horizontal(g0)
    c: DistanceX(g-1,g1) = 16
    c: DistanceY(g1,g1) = 11
    c: Coincident(g0,g3)
FEATURE [PartDesign::Revolution] Revolution
  Angle = 360
  Angle2 = 60
  Axis = (0,0,1)
  Base = (0,0,0)
  Placement = pos=(0,0,0) rot=(1,1,1;2.0944rad)
  Profile = -> Sketch024
  ReferenceAxis = -> Sketch024 [V_Axis]
  Refine = true
  Reversed = true
  Suppressed = false
  Type = 0
FEATURE [PartDesign::Chamfer] Chamfer
  Angle = 45
  Base = -> Revolution [Edge3]
  BaseFeature = -> Revolution
  ChamferType = 0
  FlipDirection = false
  Placement = pos=(0,0,0) rot=(1,1,1;2.0944rad)
  Refine = true
  Size = 1
  Size2 = 1
  SupportTransform = false
  Suppressed = false
  UseAllEdges = false
FEATURE [Sketcher::SketchObject] Sketch026
  ArcFitTolerance = 1e-06
  AttachmentSupport = -> [Chamfer]
  FullyConstrained = false
  MakeInternals = false
  MapMode = 5
  Placement = pos=(3e-16,0,-1.5) rot=(0.707107,0.707107,0;3.14159rad)
  sketch-geometry (4):
    g0: ArcOfCircle CenterX=0 CenterY=0 CenterZ=0 NormalX=0 NormalY=0 NormalZ=1 AngleXU=0 Radius=4 StartAngle=3.14159 EndAngle=6.28319
    g1: ArcOfCircle CenterX=-5e-16 CenterY=18.9943 CenterZ=0 NormalX=0 NormalY=0 NormalZ=1 AngleXU=0 Radius=4 StartAngle=0 EndAngle=3.14159
    g2: LineSegment StartX=-4 StartY=-1.3e-15 StartZ=0 EndX=-4 EndY=18.9943 EndZ=0
    g3: LineSegment StartX=4 StartY=-1e-15 StartZ=0 EndX=4 EndY=18.9943 EndZ=0
  constraints (8):
    c: Tangent(g0,g2) = 1.5708
    c: Tangent(g0,g3) = -1.5708
    c: Tangent(g1,g2) = 1.5708
    c: Tangent(g1,g3) = -1.5708
    c: Equal(g0,g1)
    c: Vertical(g3)
    c: Radius(g0) = 4
    c: Coincident(g0,g-1)
FEATURE [PartDesign::Pocket] Pocket007
  BaseFeature = -> Chamfer
  Direction = (0,0,1)
  Length = 1.5
  Length2 = 5
  Placement = pos=(0,0,0) rot=(1,1,1;2.0944rad)
  Profile = -> Sketch026
  ReferenceAxis = -> Sketch026 [N_Axis]
  Refine = true
  Suppressed = false
  Type = 0
FEATURE [PartDesign::PolarPattern] PolarPattern001
  Angle = 360
  Axis = -> Sketch026 [N_Axis]
  BaseFeature = -> Pocket007
  Mode = 0
  Occurrences = 4
  Offset = 120
  Originals = -> [Pocket007]
  Placement = pos=(0,0,0) rot=(1,1,1;2.0944rad)
  Refine = true
  Suppressed = false
  TransformMode = 0
FEATURE [Sketcher::SketchObject] Sketch027
  ArcFitTolerance = 1e-06
  AttachmentOffset = pos=(0,0,-6.5) rot=(0,0,1;0rad)
  AttachmentSupport = -> [PolarPattern001]
  ExternalGeometry = -> [PolarPattern001]
  FullyConstrained = true
  MakeInternals = false
  MapMode = 5
  Placement = pos=(3e-16,0,5) rot=(0.707107,0.707107,0;3.14159rad)
  sketch-geometry (4):
    g0: ArcOfCircle CenterX=0 CenterY=0 CenterZ=0 NormalX=0 NormalY=0 NormalZ=1 AngleXU=0 Radius=16 StartAngle=0.707584 EndAngle=0.863212
    g1: LineSegment StartX=10.4 StartY=12.1589 StartZ=0 EndX=12.1678 EndY=13.9267 EndZ=0
    g2: LineSegment StartX=12.1589 StartY=10.4 StartZ=0 EndX=13.9267 EndY=12.1678 EndZ=0
    g3: LineSegment StartX=12.1678 StartY=13.9267 StartZ=0 EndX=13.9267 EndY=12.1678 EndZ=0
  constraints (12):
    c: Distance(g1) = 2.5
    c: Angle(g-1,g1) = 0.785398
    c: Coincident(g1,g0)
    c: Distance(g2) = 2.5
    c: Angle(g-1,g2) = 0.785398
    c: Coincident(g2,g0)
    c: Coincident(g3,g1)
    c: Coincident(g3,g2)
    c: Coincident(g0,g-1)
    c: Radius(g0) = 16
    c: DistanceY(g-1,g0) = 10.4
    c: Distance(g0,g-2) = 10.4
FEATURE [PartDesign::Pad] Pad018
  BaseFeature = -> PolarPattern001
  Direction = (0,0,-1)
  Length = 3
  Length2 = 10
  Placement = pos=(0,0,0) rot=(1,1,1;2.0944rad)
  Profile = -> Sketch027
  ReferenceAxis = -> Sketch027 [N_Axis]
  Refine = true
  Suppressed = false
  Type = 0
FEATURE [PartDesign::PolarPattern] PolarPattern002
  Angle = 360
  Axis = -> Sketch027 [N_Axis]
  BaseFeature = -> Pad018
  Mode = 0
  Occurrences = 4
  Offset = 120
  Originals = -> [Pad018]
  Placement = pos=(0,0,0) rot=(1,1,1;2.0944rad)
  Refine = true
  Suppressed = false
  TransformMode = 0
FEATURE [PartDesign::Chamfer] Chamfer001
  Angle = 45
  Base = -> PolarPattern002 [Edge103]
  BaseFeature = -> PolarPattern002
  ChamferType = 0
  FlipDirection = false
  Placement = pos=(0,0,0) rot=(1,1,1;2.0944rad)
  Refine = true
  Size = 1
  Size2 = 1
  SupportTransform = false
  Suppressed = false
  UseAllEdges = false
FEATURE [Sketcher::SketchObject] Sketch028
  ArcFitTolerance = 1e-06
  AttachmentSupport = -> [Chamfer001]
  FullyConstrained = true
  MakeInternals = false
  MapMode = 5
  Placement = pos=(-2.1e-15,0,9.5) rot=(0,0,-1;1.5708rad)
  sketch-geometry (3):
    g0: LineSegment StartX=13.5 StartY=0 StartZ=0 EndX=10.6716 EndY=2.82843 EndZ=0
    g1: LineSegment StartX=10.6716 StartY=2.82843 StartZ=0 EndX=10.6716 EndY=-2.82843 EndZ=0
    g2: LineSegment StartX=10.6716 StartY=-2.82843 StartZ=0 EndX=13.5 EndY=0 EndZ=0
  constraints (9):
    c: PointOnObject(g0,g-1)
    c: Coincident(g0,g1)
    c: Vertical(g1)
    c: Coincident(g1,g2)
    c: Coincident(g2,g0)
    c: Angle(g-1,g0) = 2.35619
    c: Angle(g2,g-1) = 2.35619
    c: Distance(g0,g0) = 4
    c: DistanceX(g-1,g0) = 13.5
FEATURE [PartDesign::Pocket] Pocket008
  BaseFeature = -> Chamfer001
  Direction = (0,0,-1)
  Length = 1
  Length2 = 5
  Placement = pos=(0,0,0) rot=(1,1,1;2.0944rad)
  Profile = -> Sketch028
  ReferenceAxis = -> Sketch028 [N_Axis]
  Refine = true
  Suppressed = false
  Type = 0
FEATURE [PartDesign::PolarPattern] PolarPattern003
  Angle = 360
  Axis = -> Sketch028 [N_Axis]
  BaseFeature = -> Pocket008
  Mode = 0
  Occurrences = 4
  Offset = 120
  Originals = -> [Pocket008]
  Placement = pos=(0,0,0) rot=(1,1,1;2.0944rad)
  Refine = true
  Suppressed = false
  TransformMode = 0
FEATURE [Sketcher::SketchObject] Sketch044
  ArcFitTolerance = 1e-06
  AttachmentSupport = -> [PolarPattern003]
  FullyConstrained = false
  MakeInternals = false
  MapMode = 5
  Placement = pos=(3e-16,0,-1.5) rot=(0.707107,0.707107,0;3.14159rad)
  sketch-geometry (4):
    g0: LineSegment StartX=-9.7 StartY=1.3 StartZ=0 EndX=-9.7 EndY=-1.3 EndZ=0
    g1: LineSegment StartX=-9.7 StartY=-1.3 StartZ=0 EndX=-6.29182 EndY=-1.3 EndZ=0
    g2: LineSegment StartX=-6.29182 StartY=-1.3 StartZ=0 EndX=-6.29182 EndY=1.3 EndZ=0
    g3: LineSegment StartX=-6.29182 StartY=1.3 StartZ=0 EndX=-9.7 EndY=1.3 EndZ=0
  constraints (11):
    c: Coincident(g0,g1)
    c: Coincident(g1,g2)
    c: Coincident(g2,g3)
    c: Coincident(g3,g0)
    c: Vertical(g0)
    c: Vertical(g2)
    c: Horizontal(g1)
    c: Horizontal(g3)
    c: Distance(g-1,g3) = 1.3
    c: Distance(g-1,g1) = 1.3
    c: Distance(g0,g-2) = 9.7
FEATURE [PartDesign::Pocket] Pocket021
  BaseFeature = -> PolarPattern003
  Direction = (-1.3e-15,0,1)
  Length = 7
  Length2 = 5
  Placement = pos=(0,0,0) rot=(1,1,1;2.0944rad)
  Profile = -> Sketch044
  ReferenceAxis = -> Sketch044 [N_Axis]
  Refine = true
  Suppressed = false
  Type = 0
FEATURE [PartDesign::PolarPattern] PolarPattern010
  Angle = 360
  Axis = -> Sketch044 [N_Axis]
  BaseFeature = -> Pocket021
  Mode = 0
  Occurrences = 3
  Offset = 120
  Originals = -> [Pocket021]
  Placement = pos=(0,0,0) rot=(1,1,1;2.0944rad)
  Refine = true
  Suppressed = false
  TransformMode = 0
FEATURE [PartDesign::Body] Body007  label="Btn4Direction"
  AllowCompound = false
  Group = -> [Sketch024,Revolution,Chamfer,Sketch026,Pocket007,PolarPattern001,Sketch027,Pad018,PolarPattern002,Chamfer001,Sketch028,Pocket008,PolarPattern003,Sketch044,Pocket021,PolarPattern010]
  Origin = -> Origin009
  Placement = pos=(0,0,11.5) rot=(0,0,1;0rad)
  Tip = -> PolarPattern010
COMPONENT P6 — recipe-attached ("BtnHome", modeled in this document).
Construction recipe (the document's own serialized feature program — sketch geometry with constraints, then the solid features built on it; lengths are millimeters unless a unit is written):

FEATURE [Sketcher::SketchObject] Sketch037
  ArcFitTolerance = 1e-06
  AttachmentSupport = -> [XY_Plane010]
  FullyConstrained = true
  MakeInternals = false
  MapMode = 5
  sketch-geometry (1):
    g0: Circle CenterX=0 CenterY=0 CenterZ=0 NormalX=0 NormalY=0 NormalZ=1 AngleXU=0 Radius=7.25
  constraints (2):
    c: Diameter(g0) = 14.5
    c: Coincident(g0,g-1)
FEATURE [PartDesign::Pad] Pad023
  Direction = (0,0,1)
  Length = 11
  Length2 = 10
  Profile = -> Sketch037
  ReferenceAxis = -> Sketch037 [N_Axis]
  Refine = true
  Suppressed = false
  Type = 0
FEATURE [PartDesign::Chamfer] Chamfer003
  Angle = 45
  Base = -> Pad023 [Edge3]
  BaseFeature = -> Pad023
  ChamferType = 0
  FlipDirection = false
  Refine = true
  Size = 1
  Size2 = 1
  SupportTransform = false
  Suppressed = false
  UseAllEdges = false
FEATURE [Sketcher::SketchObject] Sketch038
  ArcFitTolerance = 1e-06
  AttachmentSupport = -> [Chamfer003]
  FullyConstrained = false
  MakeInternals = false
  MapMode = 5
  Placement = pos=(0,0,11) rot=(0,0,1;0rad)
  sketch-geometry (12):
    g0: LineSegment StartX=-3.5 StartY=1.00678 StartZ=0 EndX=-3.5 EndY=-3.31324 EndZ=0
    g1: LineSegment StartX=-3.5 StartY=-3.31324 StartZ=0 EndX=3.5 EndY=-3.31324 EndZ=0
    g2: LineSegment StartX=3.5 StartY=-3.31324 StartZ=0 EndX=3.5 EndY=1.00678 EndZ=0
    g3: LineSegment StartX=-3.5 StartY=1.00678 StartZ=0 EndX=-5.5 EndY=1.00678 EndZ=0
    g4: LineSegment StartX=-5.5 StartY=1.00678 StartZ=0 EndX=0 EndY=4.88144 EndZ=0
    g5: LineSegment StartX=0 StartY=4.88144 StartZ=0 EndX=5.5 EndY=1.00678 EndZ=0
    g6: LineSegment StartX=5.5 StartY=1.00678 StartZ=0 EndX=3.5 EndY=1.00678 EndZ=0
    g7: LineSegment StartX=-2.5 StartY=-1 StartZ=0 EndX=-0.5 EndY=-1 EndZ=0
    g8: LineSegment StartX=-0.5 StartY=-1 StartZ=0 EndX=-0.5 EndY=1 EndZ=0
    g9: LineSegment StartX=-0.5 StartY=1 StartZ=0 EndX=-2.5 EndY=1 EndZ=0
    g10: LineSegment StartX=-2.5 StartY=1 StartZ=0 EndX=-2.5 EndY=-1 EndZ=0
    g11: GeomPoint [constr] X=-1.5 Y=0 Z=0
  constraints (31):
    c: Coincident(g0,g1)
    c: Coincident(g1,g2)
    c: Vertical(g0)
    c: Vertical(g2)
    c: Horizontal(g1)
    c: Coincident(g0,g3)
    c: Coincident(g3,g4)
    c: PointOnObject(g4,g-2)
    c: Coincident(g4,g5)
    c: Coincident(g5,g6)
    c: Coincident(g6,g2)
    c: Horizontal(g6)
    c: Horizontal(g3)
    c: Horizontal(g0,g2)
    c: DistanceX(g3,g3) = 2
    c: DistanceX(g6,g6) = 2
    c: DistanceX(g0,g-1) = 3.5
    c: Distance(g1,g-2) = 3.5
    c: Coincident(g7,g8)
    c: Coincident(g8,g9)
    c: Coincident(g9,g10)
    c: Coincident(g10,g7)
    c: Horizontal(g7)
    c: Horizontal(g9)
    c: Vertical(g8)
    c: Vertical(g10)
    c: Symmetric(g9,g7,g11)
    c: Distance(g8,g10) = 2
    c: Distance(g7,g9) = 2
    c: PointOnObject(g11,g-1)
    c: DistanceX(g11,g-1) = 1.5
FEATURE [Sketcher::SketchObject] Sketch039
  ArcFitTolerance = 1e-06
  AttachmentOffset = pos=(0,0,-6.5) rot=(0,0,1;0rad)
  AttachmentSupport = -> [Chamfer003]
  ExternalGeometry = -> [Chamfer003]
  FullyConstrained = true
  MakeInternals = false
  MapMode = 5
  Placement = pos=(0,0,6.5) rot=(1,0,0;3.14159rad)
  sketch-geometry (4):
    g0: ArcOfCircle CenterX=0 CenterY=0 CenterZ=0 NormalX=0 NormalY=0 NormalZ=1 AngleXU=0 Radius=7.25 StartAngle=1.40451 EndAngle=1.73708
    g1: LineSegment StartX=-1.2 StartY=7.15 StartZ=0 EndX=-1.2 EndY=9.45 EndZ=0
    g2: LineSegment StartX=-1.2 StartY=9.45 StartZ=0 EndX=1.2 EndY=9.45 EndZ=0
    g3: LineSegment StartX=1.2 StartY=9.45 StartZ=0 EndX=1.2 EndY=7.15 EndZ=0
  constraints (12):
    c: Coincident(g0,g-1)
    c: PointOnObject(g0,g-3)
    c: Coincident(g0,g1)
    c: Coincident(g1,g2)
    c: Horizontal(g2)
    c: Coincident(g2,g3)
    c: Coincident(g3,g0)
    c: Vertical(g3)
    c: Vertical(g1)
    c: Distance(g-2,g1) = 1.2
    c: Distance(g-2,g3) = 1.2
    c: DistanceY(g3,g3) = 2.3
FEATURE [PartDesign::Pad] Pad024
  BaseFeature = -> Chamfer003
  Direction = (0,0,-1)
  Length = 2.5
  Length2 = 10
  Profile = -> Sketch039
  ReferenceAxis = -> Sketch039 [N_Axis]
  Refine = true
  Suppressed = false
  Type = 0
FEATURE [PartDesign::PolarPattern] PolarPattern008
  Angle = 360
  Axis = -> Sketch039 [N_Axis]
  BaseFeature = -> Pad024
  Mode = 0
  Occurrences = 3
  Offset = 120
  Originals = -> [Pad024]
  Refine = true
  Suppressed = false
  TransformMode = 0
FEATURE [PartDesign::Pocket] Pocket015
  BaseFeature = -> PolarPattern008
  Direction = (0,0,-1)
  Length = 1
  Length2 = 5
  Profile = -> Sketch038
  ReferenceAxis = -> Sketch038 [N_Axis]
  Refine = true
  Suppressed = false
  Type = 0
FEATURE [Sketcher::SketchObject] Sketch041
  ArcFitTolerance = 1e-06
  AttachmentSupport = -> [Pocket015]
  FullyConstrained = true
  MakeInternals = false
  MapMode = 5
  Placement = pos=(0,0,0) rot=(1,0,0;3.14159rad)
  sketch-geometry (10):
    g0: LineSegment StartX=-4 StartY=2 StartZ=0 EndX=-4 EndY=-2 EndZ=0
    g1: LineSegment StartX=-2 StartY=-4 StartZ=0 EndX=2 EndY=-4 EndZ=0
    g2: LineSegment StartX=4 StartY=-2 StartZ=0 EndX=4 EndY=2 EndZ=0
    g3: LineSegment StartX=2 StartY=4 StartZ=0 EndX=-2 EndY=4 EndZ=0
    g4: ArcOfCircle CenterX=-2 CenterY=2 CenterZ=0 NormalX=0 NormalY=0 NormalZ=1 AngleXU=0 Radius=2 StartAngle=1.5708 EndAngle=3.14159
    g5: ArcOfCircle CenterX=-2 CenterY=-2 CenterZ=0 NormalX=0 NormalY=0 NormalZ=1 AngleXU=0 Radius=2 StartAngle=3.14159 EndAngle=4.71239
    g6: ArcOfCircle CenterX=2 CenterY=-2 CenterZ=0 NormalX=0 NormalY=0 NormalZ=1 AngleXU=0 Radius=2 StartAngle=4.71239 EndAngle=6.28319
    g7: ArcOfCircle CenterX=2 CenterY=2 CenterZ=0 NormalX=0 NormalY=0 NormalZ=1 AngleXU=0 Radius=2 StartAngle=0 EndAngle=1.5708
    g8: GeomPoint [constr] X=-4 Y=4 Z=0
    g9: GeomPoint [constr] X=4 Y=-4 Z=0
  constraints (23):
    c: Tangent(g0,g4) = -1.5708
    c: Tangent(g0,g5) = -1.5708
    c: Tangent(g1,g5) = -1.5708
    c: Tangent(g1,g6) = -1.5708
    c: Tangent(g2,g6) = -1.5708
    c: Tangent(g2,g7) = -1.5708
    c: Tangent(g3,g7) = -1.5708
    c: Tangent(g3,g4) = -1.5708
    c: Vertical(g0)
    c: Vertical(g2)
    c: Horizontal(g1)
    c: Horizontal(g3)
    c: Equal(g4,g5)
    c: Equal(g5,g6)
    c: Equal(g6,g7)
    c: PointOnObject(g8,g0)
    c: PointOnObject(g8,g3)
    c: PointOnObject(g9,g1)
    c: PointOnObject(g9,g2)
    c: Distance(g0,g2) = 8
    c: Distance(g1,g3) = 8
    c: Radius(g5) = 2
    c: Symmetric(g8,g9,g-1)
FEATURE [PartDesign::Pocket] Pocket018
  BaseFeature = -> Pocket015
  Direction = (0,0,1)
  Length = 1.5
  Length2 = 5
  Profile = -> Sketch041
  ReferenceAxis = -> Sketch041 [N_Axis]
  Refine = true
  Suppressed = false
  Type = 0
FEATURE [PartDesign::Body] Body008  label="BtnHome"
  AllowCompound = false
  Group = -> [Sketch037,Pad023,Chamfer003,Sketch038,Sketch039,Pad024,PolarPattern008,Pocket015,Sketch041,Pocket018]
  Origin = -> Origin010
  Placement = pos=(20.3,23.1,10) rot=(0,0,1;0rad)
  Tip = -> Pocket018
COMPONENT P7 — geometry summary ("EasyEDA PCB Model~YX9s"; no construction recipe available for this part):
  bounding box: 88.9 x 60.9 x 1.6 mm
  tessellated surface: 12,700 triangles
  volume: 8619 mm^3 (99% of its bounding box)
  symmetry: 2-fold rotationally symmetric about the x axis; 2-fold rotationally symmetric about the y axis; 2-fold rotationally symmetric about the z axis; mirror-symmetric across its x mid-plane
COMPONENT P8 — geometry summary ("TactileSwitch001"; no construction recipe available for this part):
  bounding box: 8.4 x 8.2 x 6.0 mm
  tessellated surface: 5,566 triangles
  volume: 154 mm^3 (38% of its bounding box)
COMPONENT P9 — geometry summary ("TactileSwitch002"; no construction recipe available for this part):
  bounding box: 8.4 x 8.2 x 6.0 mm
  tessellated surface: 5,566 triangles
  volume: 154 mm^3 (38% of its bounding box)
COMPONENT P10 — geometry summary ("Micro_USB_Plug v10"; no construction recipe available for this part):
  bounding box: 83.5 x 10.6 x 6.6 mm
  tessellated surface: 32,036 triangles
  volume: 1833 mm^3 (31% of its bounding box)
  symmetry: mirror-symmetric across its x mid-plane, z mid-plane
PROVENANCE & LICENSES
A FreeCAD (.FCStd) document from a public repository crawl; recipes are the document's own serialized feature recipes (and, for linked parts, companion documents' recipes).
License: as declared in the source repository (recorded in the dataset sidecar).
